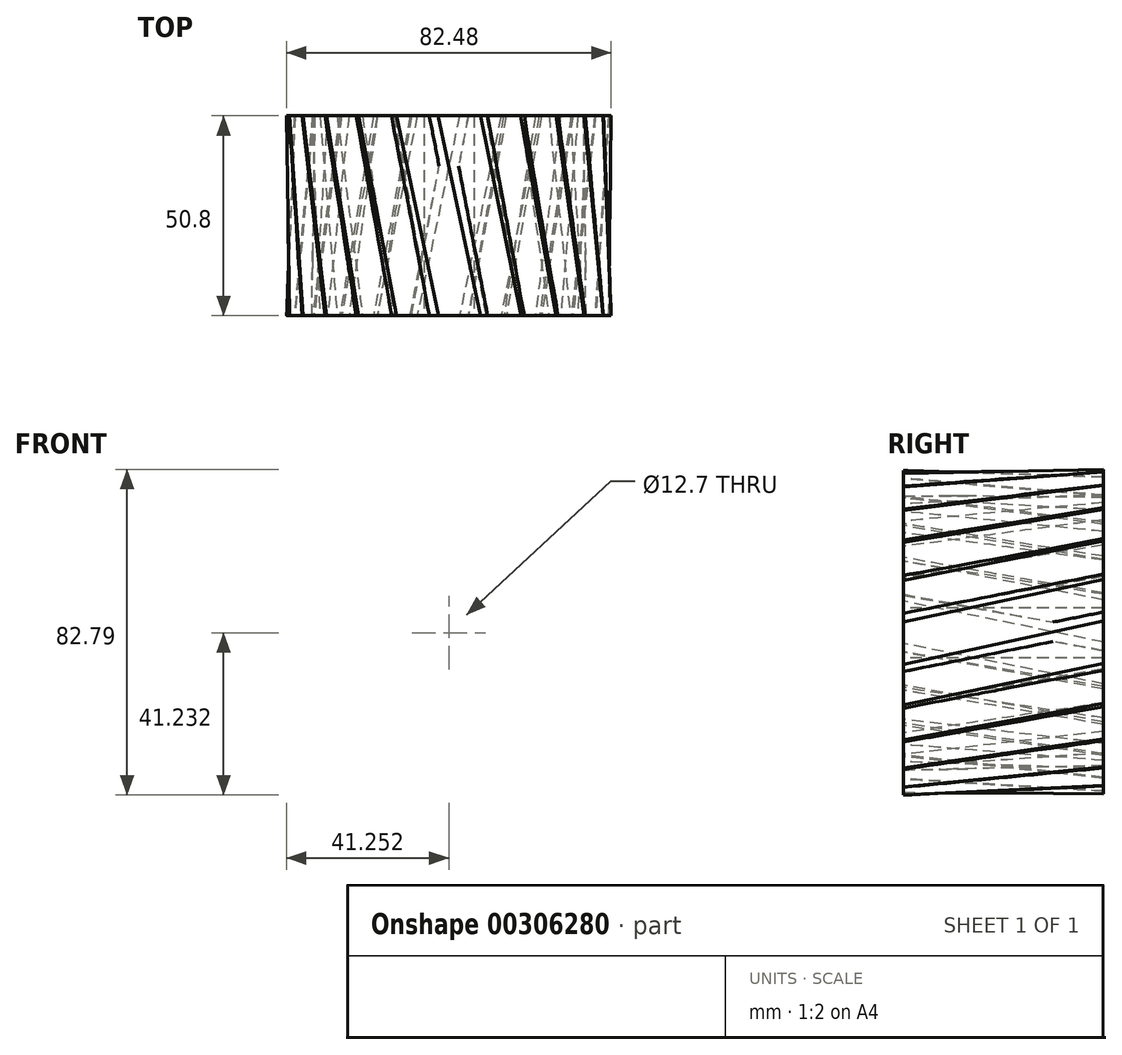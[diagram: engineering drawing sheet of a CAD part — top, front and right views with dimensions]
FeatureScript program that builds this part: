
annotation { "Feature Type Name" : "Feature", "Feature Type Description" : "" }
export const myFeature = defineFeature(function(context is Context, id is Id, definition is map)
    precondition{}
    {
        {
            var Q0;
            Q0=qCreatedBy(makeId("Front.planeOp"),FACE);
            var sketch = newSketch(context, id + "F0", { "sketchPlane" : qUnion([Q0])});
            skArc(sketch, "E0", {"start": v(-6.16, 34.38) * mm, "mid": v(-6.81, 34.25) * mm, "end": v(-7.46, 34.12) * mm});
            skArc(sketch, "E1.trimOffspring", {"start": v(-0.1, 38.36) * mm, "mid": v(-0.85, 39.78) * mm, "end": v(-1.82, 41.06) * mm});
            skLineSegment(sketch, "E2", {"start": v(0.02, 37.85) * mm, "end": v(0.11, 36.37) * mm});
            skLineSegment(sketch, "E3", {"start": v(-2.2, 41.23) * mm, "end": v(-2.7, 41.23) * mm});
            skLineSegment(sketch, "E4.MirrorCS", {"start": v(-3.2, 41.16) * mm, "end": v(-2.7, 41.23) * mm});
            skArc(sketch, "E5.MirrorCS", {"start": v(-4.9, 38.04) * mm, "mid": v(-4.35, 39.55) * mm, "end": v(-3.56, 40.95) * mm});
            skLineSegment(sketch, "E6.MirrorCS", {"start": v(-4.96, 37.52) * mm, "end": v(-4.86, 36.04) * mm});
            skPoint(sketch, "E7.orphan", {"position": v(0.33, 33.11) * mm});
            skPoint(sketch, "E8.orphan", {"position": v(-4.65, 32.79) * mm});
            skPoint(sketch, "E9.visualSharp", {"position": v(0.2, 34.92) * mm});
            skArc(sketch, "E9.filletArc", {"start": v(0.11, 36.37) * mm, "mid": v(0.59, 35.34) * mm, "end": v(1.62, 34.89) * mm});
            skPoint(sketch, "E10.visualSharp", {"position": v(-4.76, 34.6) * mm});
            skArc(sketch, "E10.filletArc", {"start": v(-6.16, 34.38) * mm, "mid": v(-5.2, 34.96) * mm, "end": v(-4.86, 36.04) * mm});
            skPoint(sketch, "E11.visualSharp", {"position": v(-3.43, 41.13) * mm});
            skArc(sketch, "E11.filletArc", {"start": v(-3.2, 41.16) * mm, "mid": v(-3.4, 41.1) * mm, "end": v(-3.56, 40.95) * mm});
            skPoint(sketch, "E12.visualSharp", {"position": v(-1.97, 41.23) * mm});
            skArc(sketch, "E12.filletArc", {"start": v(-1.82, 41.06) * mm, "mid": v(-1.99, 41.18) * mm, "end": v(-2.2, 41.23) * mm});
            skPoint(sketch, "E13.visualSharp", {"position": v(-4.97, 37.77) * mm});
            skArc(sketch, "E13.filletArc", {"start": v(-4.9, 38.04) * mm, "mid": v(-4.95, 37.78) * mm, "end": v(-4.96, 37.52) * mm});
            skPoint(sketch, "E14.visualSharp", {"position": v(0, 38.1) * mm});
            skArc(sketch, "E14.filletArc", {"start": v(0.02, 37.85) * mm, "mid": v(-0.02, 38.1) * mm, "end": v(-0.1, 38.36) * mm});
            skArc(sketch, "E15.1.0", {"start": v(-9.3, 35.16) * mm, "mid": v(-8.58, 34.29) * mm, "end": v(-7.46, 34.12) * mm});
            skArc(sketch, "E15.1.1", {"start": v(-14.85, 31.61) * mm, "mid": v(-14.07, 32.43) * mm, "end": v(-14.02, 33.56) * mm});
            skLineSegment(sketch, "E15.1.2", {"start": v(-9.78, 36.56) * mm, "end": v(-9.3, 35.16) * mm});
            skLineSegment(sketch, "E15.1.3", {"start": v(-14.5, 34.96) * mm, "end": v(-14.02, 33.56) * mm});
            skPoint(sketch, "E15.1.4", {"position": v(-12.58, 39.31) * mm});
            skPoint(sketch, "E15.1.5", {"position": v(-13.96, 38.84) * mm});
            skArc(sketch, "E15.1.6", {"start": v(-14.58, 35.48) * mm, "mid": v(-14.44, 37.08) * mm, "end": v(-14.03, 38.63) * mm});
            skPoint(sketch, "E15.1.7", {"position": v(-14.58, 35.2) * mm});
            skPoint(sketch, "E15.1.8", {"position": v(-9.86, 36.8) * mm});
            skArc(sketch, "E15.1.9", {"start": v(-10.03, 37.02) * mm, "mid": v(-11.11, 38.2) * mm, "end": v(-12.38, 39.2) * mm});
            skLineSegment(sketch, "E15.1.10", {"start": v(-12.79, 39.26) * mm, "end": v(-13.28, 39.12) * mm});
            skLineSegment(sketch, "E15.1.11", {"start": v(-13.75, 38.93) * mm, "end": v(-13.28, 39.12) * mm});
            skArc(sketch, "E15.1.12", {"start": v(-9.78, 36.56) * mm, "mid": v(-9.88, 36.8) * mm, "end": v(-10.03, 37.02) * mm});
            skArc(sketch, "E15.1.13", {"start": v(-13.75, 38.93) * mm, "mid": v(-13.92, 38.8) * mm, "end": v(-14.03, 38.63) * mm});
            skArc(sketch, "E15.1.14", {"start": v(-14.58, 35.48) * mm, "mid": v(-14.56, 35.22) * mm, "end": v(-14.5, 34.96) * mm});
            skArc(sketch, "E15.1.15", {"start": v(-12.38, 39.2) * mm, "mid": v(-12.58, 39.27) * mm, "end": v(-12.79, 39.26) * mm});
            skArc(sketch, "E15.2.0", {"start": v(-18.09, 31.55) * mm, "mid": v(-17.16, 30.9) * mm, "end": v(-16.04, 31.03) * mm});
            skArc(sketch, "E15.2.1", {"start": v(-22.53, 26.69) * mm, "mid": v(-21.98, 27.68) * mm, "end": v(-22.23, 28.78) * mm});
            skLineSegment(sketch, "E15.2.2", {"start": v(-18.9, 32.79) * mm, "end": v(-18.09, 31.55) * mm});
            skLineSegment(sketch, "E15.2.3", {"start": v(-23.05, 30.02) * mm, "end": v(-22.23, 28.78) * mm});
            skPoint(sketch, "E15.2.4", {"position": v(-22.32, 34.72) * mm});
            skPoint(sketch, "E15.2.5", {"position": v(-23.53, 33.9) * mm});
            skArc(sketch, "E15.2.6", {"start": v(-23.27, 30.5) * mm, "mid": v(-23.55, 32.08) * mm, "end": v(-23.55, 33.68) * mm});
            skPoint(sketch, "E15.2.7", {"position": v(-23.2, 30.23) * mm});
            skPoint(sketch, "E15.2.8", {"position": v(-19.05, 33) * mm});
            skArc(sketch, "E15.2.9", {"start": v(-19.27, 33.17) * mm, "mid": v(-20.62, 34.03) * mm, "end": v(-22.1, 34.65) * mm});
            skLineSegment(sketch, "E15.2.10", {"start": v(-22.51, 34.6) * mm, "end": v(-22.95, 34.35) * mm});
            skLineSegment(sketch, "E15.2.11", {"start": v(-23.36, 34.04) * mm, "end": v(-22.95, 34.35) * mm});
            skArc(sketch, "E15.2.12", {"start": v(-18.9, 32.79) * mm, "mid": v(-19.07, 33) * mm, "end": v(-19.27, 33.17) * mm});
            skArc(sketch, "E15.2.13", {"start": v(-23.36, 34.04) * mm, "mid": v(-23.5, 33.88) * mm, "end": v(-23.55, 33.68) * mm});
            skArc(sketch, "E15.2.14", {"start": v(-23.27, 30.5) * mm, "mid": v(-23.18, 30.25) * mm, "end": v(-23.05, 30.02) * mm});
            skArc(sketch, "E15.2.15", {"start": v(-22.1, 34.65) * mm, "mid": v(-22.31, 34.67) * mm, "end": v(-22.51, 34.6) * mm});
            skArc(sketch, "E15.3.0", {"start": v(-25.64, 25.8) * mm, "mid": v(-24.57, 25.4) * mm, "end": v(-23.52, 25.82) * mm});
            skArc(sketch, "E15.3.1", {"start": v(-28.67, 19.95) * mm, "mid": v(-28.4, 21.05) * mm, "end": v(-28.92, 22.05) * mm});
            skLineSegment(sketch, "E15.3.2", {"start": v(-26.75, 26.77) * mm, "end": v(-25.64, 25.8) * mm});
            skLineSegment(sketch, "E15.3.3", {"start": v(-30.04, 23.03) * mm, "end": v(-28.92, 22.05) * mm});
            skPoint(sketch, "E15.3.4", {"position": v(-30.55, 27.76) * mm});
            skPoint(sketch, "E15.3.5", {"position": v(-31.5, 26.66) * mm});
            skArc(sketch, "E15.3.6", {"start": v(-30.37, 23.43) * mm, "mid": v(-31.05, 24.89) * mm, "end": v(-31.47, 26.44) * mm});
            skPoint(sketch, "E15.3.7", {"position": v(-30.23, 23.2) * mm});
            skPoint(sketch, "E15.3.8", {"position": v(-26.94, 26.94) * mm});
            skArc(sketch, "E15.3.9", {"start": v(-27.2, 27.05) * mm, "mid": v(-28.73, 27.53) * mm, "end": v(-30.32, 27.75) * mm});
            skLineSegment(sketch, "E15.3.10", {"start": v(-30.7, 27.6) * mm, "end": v(-31.06, 27.24) * mm});
            skLineSegment(sketch, "E15.3.11", {"start": v(-31.37, 26.84) * mm, "end": v(-31.06, 27.24) * mm});
            skArc(sketch, "E15.3.12", {"start": v(-26.75, 26.77) * mm, "mid": v(-26.96, 26.93) * mm, "end": v(-27.2, 27.05) * mm});
            skArc(sketch, "E15.3.13", {"start": v(-31.37, 26.84) * mm, "mid": v(-31.46, 26.65) * mm, "end": v(-31.47, 26.44) * mm});
            skArc(sketch, "E15.3.14", {"start": v(-30.37, 23.43) * mm, "mid": v(-30.22, 23.22) * mm, "end": v(-30.04, 23.03) * mm});
            skArc(sketch, "E15.3.15", {"start": v(-30.32, 27.75) * mm, "mid": v(-30.53, 27.72) * mm, "end": v(-30.7, 27.6) * mm});
            skArc(sketch, "E15.4.0", {"start": v(-31.44, 18.28) * mm, "mid": v(-30.31, 18.18) * mm, "end": v(-29.4, 18.85) * mm});
            skArc(sketch, "E15.4.1", {"start": v(-32.85, 11.85) * mm, "mid": v(-32.87, 12.98) * mm, "end": v(-33.64, 13.81) * mm});
            skLineSegment(sketch, "E15.4.2", {"start": v(-32.77, 18.94) * mm, "end": v(-31.44, 18.28) * mm});
            skLineSegment(sketch, "E15.4.3", {"start": v(-34.97, 14.47) * mm, "end": v(-33.64, 13.81) * mm});
            skPoint(sketch, "E15.4.4", {"position": v(-36.7, 18.9) * mm});
            skPoint(sketch, "E15.4.5", {"position": v(-37.33, 17.6) * mm});
            skArc(sketch, "E15.4.6", {"start": v(-35.4, 14.77) * mm, "mid": v(-36.43, 16) * mm, "end": v(-37.24, 17.4) * mm});
            skPoint(sketch, "E15.4.7", {"position": v(-35.2, 14.58) * mm});
            skPoint(sketch, "E15.4.8", {"position": v(-33, 19.05) * mm});
            skArc(sketch, "E15.4.9", {"start": v(-33.27, 19.09) * mm, "mid": v(-34.87, 19.16) * mm, "end": v(-36.47, 18.96) * mm});
            skLineSegment(sketch, "E15.4.10", {"start": v(-36.8, 18.71) * mm, "end": v(-37.06, 18.27) * mm});
            skLineSegment(sketch, "E15.4.11", {"start": v(-37.25, 17.8) * mm, "end": v(-37.06, 18.27) * mm});
            skArc(sketch, "E15.4.12", {"start": v(-32.77, 18.94) * mm, "mid": v(-33.01, 19.03) * mm, "end": v(-33.27, 19.09) * mm});
            skArc(sketch, "E15.4.13", {"start": v(-37.25, 17.8) * mm, "mid": v(-37.29, 17.6) * mm, "end": v(-37.24, 17.4) * mm});
            skArc(sketch, "E15.4.14", {"start": v(-35.4, 14.77) * mm, "mid": v(-35.2, 14.6) * mm, "end": v(-34.97, 14.47) * mm});
            skArc(sketch, "E15.4.15", {"start": v(-36.47, 18.96) * mm, "mid": v(-36.66, 18.87) * mm, "end": v(-36.8, 18.71) * mm});
            skArc(sketch, "E15.5.0", {"start": v(-35.1, 9.52) * mm, "mid": v(-33.98, 9.71) * mm, "end": v(-33.28, 10.6) * mm});
            skArc(sketch, "E15.5.1", {"start": v(-34.8, 2.94) * mm, "mid": v(-35.11, 4.03) * mm, "end": v(-36.07, 4.63) * mm});
            skLineSegment(sketch, "E15.5.2", {"start": v(-36.55, 9.81) * mm, "end": v(-35.1, 9.52) * mm});
            skLineSegment(sketch, "E15.5.3", {"start": v(-37.53, 4.92) * mm, "end": v(-36.07, 4.63) * mm});
            skPoint(sketch, "E15.5.4", {"position": v(-40.33, 8.77) * mm});
            skPoint(sketch, "E15.5.5", {"position": v(-40.62, 7.34) * mm});
            skArc(sketch, "E15.5.6", {"start": v(-38.02, 5.1) * mm, "mid": v(-39.33, 6.03) * mm, "end": v(-40.47, 7.16) * mm});
            skPoint(sketch, "E15.5.7", {"position": v(-37.77, 4.97) * mm});
            skPoint(sketch, "E15.5.8", {"position": v(-36.8, 9.86) * mm});
            skArc(sketch, "E15.5.9", {"start": v(-37.08, 9.83) * mm, "mid": v(-38.64, 9.48) * mm, "end": v(-40.13, 8.87) * mm});
            skLineSegment(sketch, "E15.5.10", {"start": v(-40.4, 8.55) * mm, "end": v(-40.52, 8.06) * mm});
            skLineSegment(sketch, "E15.5.11", {"start": v(-40.59, 7.56) * mm, "end": v(-40.52, 8.06) * mm});
            skArc(sketch, "E15.5.12", {"start": v(-36.55, 9.81) * mm, "mid": v(-36.81, 9.84) * mm, "end": v(-37.08, 9.83) * mm});
            skArc(sketch, "E15.5.13", {"start": v(-40.59, 7.56) * mm, "mid": v(-40.57, 7.35) * mm, "end": v(-40.47, 7.16) * mm});
            skArc(sketch, "E15.5.14", {"start": v(-38.02, 5.1) * mm, "mid": v(-37.78, 5) * mm, "end": v(-37.53, 4.92) * mm});
            skArc(sketch, "E15.5.15", {"start": v(-40.13, 8.87) * mm, "mid": v(-40.3, 8.74) * mm, "end": v(-40.4, 8.55) * mm});
            skArc(sketch, "E15.6.0", {"start": v(-36.37, 0.11) * mm, "mid": v(-35.34, 0.59) * mm, "end": v(-34.89, 1.62) * mm});
            skArc(sketch, "E15.6.1", {"start": v(-34.38, -6.16) * mm, "mid": v(-34.96, -5.2) * mm, "end": v(-36.04, -4.86) * mm});
            skLineSegment(sketch, "E15.6.2", {"start": v(-37.85, 0.02) * mm, "end": v(-36.37, 0.11) * mm});
            skLineSegment(sketch, "E15.6.3", {"start": v(-37.52, -4.96) * mm, "end": v(-36.04, -4.86) * mm});
            skPoint(sketch, "E15.6.4", {"position": v(-41.23, -1.97) * mm});
            skPoint(sketch, "E15.6.5", {"position": v(-41.13, -3.43) * mm});
            skArc(sketch, "E15.6.6", {"start": v(-38.04, -4.9) * mm, "mid": v(-39.55, -4.35) * mm, "end": v(-40.95, -3.56) * mm});
            skPoint(sketch, "E15.6.7", {"position": v(-37.77, -4.97) * mm});
            skPoint(sketch, "E15.6.8", {"position": v(-38.1, 0) * mm});
            skArc(sketch, "E15.6.9", {"start": v(-38.36, -0.1) * mm, "mid": v(-39.78, -0.85) * mm, "end": v(-41.06, -1.82) * mm});
            skLineSegment(sketch, "E15.6.10", {"start": v(-41.23, -2.2) * mm, "end": v(-41.23, -2.7) * mm});
            skLineSegment(sketch, "E15.6.11", {"start": v(-41.16, -3.2) * mm, "end": v(-41.23, -2.7) * mm});
            skArc(sketch, "E15.6.12", {"start": v(-37.85, 0.02) * mm, "mid": v(-38.1, -0.02) * mm, "end": v(-38.36, -0.1) * mm});
            skArc(sketch, "E15.6.13", {"start": v(-41.16, -3.2) * mm, "mid": v(-41.1, -3.4) * mm, "end": v(-40.95, -3.56) * mm});
            skArc(sketch, "E15.6.14", {"start": v(-38.04, -4.9) * mm, "mid": v(-37.78, -4.95) * mm, "end": v(-37.52, -4.96) * mm});
            skArc(sketch, "E15.6.15", {"start": v(-41.06, -1.82) * mm, "mid": v(-41.18, -1.99) * mm, "end": v(-41.23, -2.2) * mm});
            skArc(sketch, "E15.7.0", {"start": v(-35.16, -9.3) * mm, "mid": v(-34.29, -8.58) * mm, "end": v(-34.12, -7.46) * mm});
            skArc(sketch, "E15.7.1", {"start": v(-31.61, -14.85) * mm, "mid": v(-32.43, -14.07) * mm, "end": v(-33.56, -14.02) * mm});
            skLineSegment(sketch, "E15.7.2", {"start": v(-36.56, -9.78) * mm, "end": v(-35.16, -9.3) * mm});
            skLineSegment(sketch, "E15.7.3", {"start": v(-34.96, -14.5) * mm, "end": v(-33.56, -14.02) * mm});
            skPoint(sketch, "E15.7.4", {"position": v(-39.31, -12.58) * mm});
            skPoint(sketch, "E15.7.5", {"position": v(-38.84, -13.96) * mm});
            skArc(sketch, "E15.7.6", {"start": v(-35.48, -14.58) * mm, "mid": v(-37.08, -14.44) * mm, "end": v(-38.63, -14.03) * mm});
            skPoint(sketch, "E15.7.7", {"position": v(-35.2, -14.58) * mm});
            skPoint(sketch, "E15.7.8", {"position": v(-36.8, -9.86) * mm});
            skArc(sketch, "E15.7.9", {"start": v(-37.02, -10.03) * mm, "mid": v(-38.2, -11.11) * mm, "end": v(-39.2, -12.38) * mm});
            skLineSegment(sketch, "E15.7.10", {"start": v(-39.26, -12.79) * mm, "end": v(-39.12, -13.28) * mm});
            skLineSegment(sketch, "E15.7.11", {"start": v(-38.93, -13.75) * mm, "end": v(-39.12, -13.28) * mm});
            skArc(sketch, "E15.7.12", {"start": v(-36.56, -9.78) * mm, "mid": v(-36.8, -9.88) * mm, "end": v(-37.02, -10.03) * mm});
            skArc(sketch, "E15.7.13", {"start": v(-38.93, -13.75) * mm, "mid": v(-38.8, -13.92) * mm, "end": v(-38.63, -14.03) * mm});
            skArc(sketch, "E15.7.14", {"start": v(-35.48, -14.58) * mm, "mid": v(-35.22, -14.56) * mm, "end": v(-34.96, -14.5) * mm});
            skArc(sketch, "E15.7.15", {"start": v(-39.2, -12.38) * mm, "mid": v(-39.27, -12.58) * mm, "end": v(-39.26, -12.79) * mm});
            skArc(sketch, "E15.8.0", {"start": v(-31.55, -18.09) * mm, "mid": v(-30.9, -17.16) * mm, "end": v(-31.03, -16.04) * mm});
            skArc(sketch, "E15.8.1", {"start": v(-26.69, -22.53) * mm, "mid": v(-27.68, -21.98) * mm, "end": v(-28.78, -22.23) * mm});
            skLineSegment(sketch, "E15.8.2", {"start": v(-32.79, -18.9) * mm, "end": v(-31.55, -18.09) * mm});
            skLineSegment(sketch, "E15.8.3", {"start": v(-30.02, -23.05) * mm, "end": v(-28.78, -22.23) * mm});
            skPoint(sketch, "E15.8.4", {"position": v(-34.72, -22.32) * mm});
            skPoint(sketch, "E15.8.5", {"position": v(-33.9, -23.53) * mm});
            skArc(sketch, "E15.8.6", {"start": v(-30.5, -23.27) * mm, "mid": v(-32.08, -23.55) * mm, "end": v(-33.68, -23.55) * mm});
            skPoint(sketch, "E15.8.7", {"position": v(-30.23, -23.2) * mm});
            skPoint(sketch, "E15.8.8", {"position": v(-33, -19.05) * mm});
            skArc(sketch, "E15.8.9", {"start": v(-33.17, -19.27) * mm, "mid": v(-34.03, -20.62) * mm, "end": v(-34.65, -22.1) * mm});
            skLineSegment(sketch, "E15.8.10", {"start": v(-34.6, -22.51) * mm, "end": v(-34.35, -22.95) * mm});
            skLineSegment(sketch, "E15.8.11", {"start": v(-34.04, -23.36) * mm, "end": v(-34.35, -22.95) * mm});
            skArc(sketch, "E15.8.12", {"start": v(-32.79, -18.9) * mm, "mid": v(-33, -19.07) * mm, "end": v(-33.17, -19.27) * mm});
            skArc(sketch, "E15.8.13", {"start": v(-34.04, -23.36) * mm, "mid": v(-33.88, -23.5) * mm, "end": v(-33.68, -23.55) * mm});
            skArc(sketch, "E15.8.14", {"start": v(-30.5, -23.27) * mm, "mid": v(-30.25, -23.18) * mm, "end": v(-30.02, -23.05) * mm});
            skArc(sketch, "E15.8.15", {"start": v(-34.65, -22.1) * mm, "mid": v(-34.67, -22.31) * mm, "end": v(-34.6, -22.51) * mm});
            skArc(sketch, "E15.9.0", {"start": v(-25.8, -25.64) * mm, "mid": v(-25.4, -24.57) * mm, "end": v(-25.82, -23.52) * mm});
            skArc(sketch, "E15.9.1", {"start": v(-19.95, -28.67) * mm, "mid": v(-21.05, -28.4) * mm, "end": v(-22.05, -28.92) * mm});
            skLineSegment(sketch, "E15.9.2", {"start": v(-26.77, -26.75) * mm, "end": v(-25.8, -25.64) * mm});
            skLineSegment(sketch, "E15.9.3", {"start": v(-23.03, -30.04) * mm, "end": v(-22.05, -28.92) * mm});
            skPoint(sketch, "E15.9.4", {"position": v(-27.76, -30.55) * mm});
            skPoint(sketch, "E15.9.5", {"position": v(-26.66, -31.5) * mm});
            skArc(sketch, "E15.9.6", {"start": v(-23.43, -30.37) * mm, "mid": v(-24.89, -31.05) * mm, "end": v(-26.44, -31.47) * mm});
            skPoint(sketch, "E15.9.7", {"position": v(-23.2, -30.23) * mm});
            skPoint(sketch, "E15.9.8", {"position": v(-26.94, -26.94) * mm});
            skArc(sketch, "E15.9.9", {"start": v(-27.05, -27.2) * mm, "mid": v(-27.53, -28.73) * mm, "end": v(-27.75, -30.32) * mm});
            skLineSegment(sketch, "E15.9.10", {"start": v(-27.6, -30.7) * mm, "end": v(-27.24, -31.06) * mm});
            skLineSegment(sketch, "E15.9.11", {"start": v(-26.84, -31.37) * mm, "end": v(-27.24, -31.06) * mm});
            skArc(sketch, "E15.9.12", {"start": v(-26.77, -26.75) * mm, "mid": v(-26.93, -26.96) * mm, "end": v(-27.05, -27.2) * mm});
            skArc(sketch, "E15.9.13", {"start": v(-26.84, -31.37) * mm, "mid": v(-26.65, -31.46) * mm, "end": v(-26.44, -31.47) * mm});
            skArc(sketch, "E15.9.14", {"start": v(-23.43, -30.37) * mm, "mid": v(-23.22, -30.22) * mm, "end": v(-23.03, -30.04) * mm});
            skArc(sketch, "E15.9.15", {"start": v(-27.75, -30.32) * mm, "mid": v(-27.72, -30.53) * mm, "end": v(-27.6, -30.7) * mm});
            skArc(sketch, "E15.10.0", {"start": v(-18.28, -31.44) * mm, "mid": v(-18.18, -30.31) * mm, "end": v(-18.85, -29.4) * mm});
            skArc(sketch, "E15.10.1", {"start": v(-11.85, -32.85) * mm, "mid": v(-12.98, -32.87) * mm, "end": v(-13.81, -33.64) * mm});
            skLineSegment(sketch, "E15.10.2", {"start": v(-18.94, -32.77) * mm, "end": v(-18.28, -31.44) * mm});
            skLineSegment(sketch, "E15.10.3", {"start": v(-14.47, -34.97) * mm, "end": v(-13.81, -33.64) * mm});
            skPoint(sketch, "E15.10.4", {"position": v(-18.9, -36.7) * mm});
            skPoint(sketch, "E15.10.5", {"position": v(-17.6, -37.33) * mm});
            skArc(sketch, "E15.10.6", {"start": v(-14.77, -35.4) * mm, "mid": v(-16, -36.43) * mm, "end": v(-17.4, -37.24) * mm});
            skPoint(sketch, "E15.10.7", {"position": v(-14.58, -35.2) * mm});
            skPoint(sketch, "E15.10.8", {"position": v(-19.05, -33) * mm});
            skArc(sketch, "E15.10.9", {"start": v(-19.09, -33.27) * mm, "mid": v(-19.16, -34.87) * mm, "end": v(-18.96, -36.47) * mm});
            skLineSegment(sketch, "E15.10.10", {"start": v(-18.71, -36.8) * mm, "end": v(-18.27, -37.06) * mm});
            skLineSegment(sketch, "E15.10.11", {"start": v(-17.8, -37.25) * mm, "end": v(-18.27, -37.06) * mm});
            skArc(sketch, "E15.10.12", {"start": v(-18.94, -32.77) * mm, "mid": v(-19.03, -33.01) * mm, "end": v(-19.09, -33.27) * mm});
            skArc(sketch, "E15.10.13", {"start": v(-17.8, -37.25) * mm, "mid": v(-17.6, -37.29) * mm, "end": v(-17.4, -37.24) * mm});
            skArc(sketch, "E15.10.14", {"start": v(-14.77, -35.4) * mm, "mid": v(-14.6, -35.2) * mm, "end": v(-14.47, -34.97) * mm});
            skArc(sketch, "E15.10.15", {"start": v(-18.96, -36.47) * mm, "mid": v(-18.87, -36.66) * mm, "end": v(-18.71, -36.8) * mm});
            skArc(sketch, "E15.11.0", {"start": v(-9.52, -35.1) * mm, "mid": v(-9.71, -33.98) * mm, "end": v(-10.6, -33.28) * mm});
            skArc(sketch, "E15.11.1", {"start": v(-2.94, -34.8) * mm, "mid": v(-4.03, -35.11) * mm, "end": v(-4.63, -36.07) * mm});
            skLineSegment(sketch, "E15.11.2", {"start": v(-9.81, -36.55) * mm, "end": v(-9.52, -35.1) * mm});
            skLineSegment(sketch, "E15.11.3", {"start": v(-4.92, -37.53) * mm, "end": v(-4.63, -36.07) * mm});
            skPoint(sketch, "E15.11.4", {"position": v(-8.77, -40.33) * mm});
            skPoint(sketch, "E15.11.5", {"position": v(-7.34, -40.62) * mm});
            skArc(sketch, "E15.11.6", {"start": v(-5.1, -38.02) * mm, "mid": v(-6.03, -39.33) * mm, "end": v(-7.16, -40.47) * mm});
            skPoint(sketch, "E15.11.7", {"position": v(-4.97, -37.77) * mm});
            skPoint(sketch, "E15.11.8", {"position": v(-9.86, -36.8) * mm});
            skArc(sketch, "E15.11.9", {"start": v(-9.83, -37.08) * mm, "mid": v(-9.48, -38.64) * mm, "end": v(-8.87, -40.13) * mm});
            skLineSegment(sketch, "E15.11.10", {"start": v(-8.55, -40.4) * mm, "end": v(-8.06, -40.52) * mm});
            skLineSegment(sketch, "E15.11.11", {"start": v(-7.56, -40.59) * mm, "end": v(-8.06, -40.52) * mm});
            skArc(sketch, "E15.11.12", {"start": v(-9.81, -36.55) * mm, "mid": v(-9.84, -36.81) * mm, "end": v(-9.83, -37.08) * mm});
            skArc(sketch, "E15.11.13", {"start": v(-7.56, -40.59) * mm, "mid": v(-7.35, -40.57) * mm, "end": v(-7.16, -40.47) * mm});
            skArc(sketch, "E15.11.14", {"start": v(-5.1, -38.02) * mm, "mid": v(-5, -37.78) * mm, "end": v(-4.92, -37.53) * mm});
            skArc(sketch, "E15.11.15", {"start": v(-8.87, -40.13) * mm, "mid": v(-8.74, -40.3) * mm, "end": v(-8.55, -40.4) * mm});
            skArc(sketch, "E15.12.0", {"start": v(-0.11, -36.37) * mm, "mid": v(-0.59, -35.34) * mm, "end": v(-1.62, -34.89) * mm});
            skArc(sketch, "E15.12.1", {"start": v(6.16, -34.38) * mm, "mid": v(5.2, -34.96) * mm, "end": v(4.86, -36.04) * mm});
            skLineSegment(sketch, "E15.12.2", {"start": v(-0.02, -37.85) * mm, "end": v(-0.11, -36.37) * mm});
            skLineSegment(sketch, "E15.12.3", {"start": v(4.96, -37.52) * mm, "end": v(4.86, -36.04) * mm});
            skPoint(sketch, "E15.12.4", {"position": v(1.97, -41.23) * mm});
            skPoint(sketch, "E15.12.5", {"position": v(3.43, -41.13) * mm});
            skArc(sketch, "E15.12.6", {"start": v(4.9, -38.04) * mm, "mid": v(4.35, -39.55) * mm, "end": v(3.56, -40.95) * mm});
            skPoint(sketch, "E15.12.7", {"position": v(4.97, -37.77) * mm});
            skPoint(sketch, "E15.12.8", {"position": v(0, -38.1) * mm});
            skArc(sketch, "E15.12.9", {"start": v(0.1, -38.36) * mm, "mid": v(0.85, -39.78) * mm, "end": v(1.82, -41.06) * mm});
            skLineSegment(sketch, "E15.12.10", {"start": v(2.2, -41.23) * mm, "end": v(2.7, -41.23) * mm});
            skLineSegment(sketch, "E15.12.11", {"start": v(3.2, -41.16) * mm, "end": v(2.7, -41.23) * mm});
            skArc(sketch, "E15.12.12", {"start": v(-0.02, -37.85) * mm, "mid": v(0.02, -38.1) * mm, "end": v(0.1, -38.36) * mm});
            skArc(sketch, "E15.12.13", {"start": v(3.2, -41.16) * mm, "mid": v(3.4, -41.1) * mm, "end": v(3.56, -40.95) * mm});
            skArc(sketch, "E15.12.14", {"start": v(4.9, -38.04) * mm, "mid": v(4.95, -37.78) * mm, "end": v(4.96, -37.52) * mm});
            skArc(sketch, "E15.12.15", {"start": v(1.82, -41.06) * mm, "mid": v(1.99, -41.18) * mm, "end": v(2.2, -41.23) * mm});
            skArc(sketch, "E15.13.0", {"start": v(9.3, -35.16) * mm, "mid": v(8.58, -34.29) * mm, "end": v(7.46, -34.12) * mm});
            skArc(sketch, "E15.13.1", {"start": v(14.85, -31.61) * mm, "mid": v(14.07, -32.43) * mm, "end": v(14.02, -33.56) * mm});
            skLineSegment(sketch, "E15.13.2", {"start": v(9.78, -36.56) * mm, "end": v(9.3, -35.16) * mm});
            skLineSegment(sketch, "E15.13.3", {"start": v(14.5, -34.96) * mm, "end": v(14.02, -33.56) * mm});
            skPoint(sketch, "E15.13.4", {"position": v(12.58, -39.31) * mm});
            skPoint(sketch, "E15.13.5", {"position": v(13.96, -38.84) * mm});
            skArc(sketch, "E15.13.6", {"start": v(14.58, -35.48) * mm, "mid": v(14.44, -37.08) * mm, "end": v(14.03, -38.63) * mm});
            skPoint(sketch, "E15.13.7", {"position": v(14.58, -35.2) * mm});
            skPoint(sketch, "E15.13.8", {"position": v(9.86, -36.8) * mm});
            skArc(sketch, "E15.13.9", {"start": v(10.03, -37.02) * mm, "mid": v(11.11, -38.2) * mm, "end": v(12.38, -39.2) * mm});
            skLineSegment(sketch, "E15.13.10", {"start": v(12.79, -39.26) * mm, "end": v(13.28, -39.12) * mm});
            skLineSegment(sketch, "E15.13.11", {"start": v(13.75, -38.93) * mm, "end": v(13.28, -39.12) * mm});
            skArc(sketch, "E15.13.12", {"start": v(9.78, -36.56) * mm, "mid": v(9.88, -36.8) * mm, "end": v(10.03, -37.02) * mm});
            skArc(sketch, "E15.13.13", {"start": v(13.75, -38.93) * mm, "mid": v(13.92, -38.8) * mm, "end": v(14.03, -38.63) * mm});
            skArc(sketch, "E15.13.14", {"start": v(14.58, -35.48) * mm, "mid": v(14.56, -35.22) * mm, "end": v(14.5, -34.96) * mm});
            skArc(sketch, "E15.13.15", {"start": v(12.38, -39.2) * mm, "mid": v(12.58, -39.27) * mm, "end": v(12.79, -39.26) * mm});
            skArc(sketch, "E15.14.0", {"start": v(18.09, -31.55) * mm, "mid": v(17.16, -30.9) * mm, "end": v(16.04, -31.03) * mm});
            skArc(sketch, "E15.14.1", {"start": v(22.53, -26.69) * mm, "mid": v(21.98, -27.68) * mm, "end": v(22.23, -28.78) * mm});
            skLineSegment(sketch, "E15.14.2", {"start": v(18.9, -32.79) * mm, "end": v(18.09, -31.55) * mm});
            skLineSegment(sketch, "E15.14.3", {"start": v(23.05, -30.02) * mm, "end": v(22.23, -28.78) * mm});
            skPoint(sketch, "E15.14.4", {"position": v(22.32, -34.72) * mm});
            skPoint(sketch, "E15.14.5", {"position": v(23.53, -33.9) * mm});
            skArc(sketch, "E15.14.6", {"start": v(23.27, -30.5) * mm, "mid": v(23.55, -32.08) * mm, "end": v(23.55, -33.68) * mm});
            skPoint(sketch, "E15.14.7", {"position": v(23.2, -30.23) * mm});
            skPoint(sketch, "E15.14.8", {"position": v(19.05, -33) * mm});
            skArc(sketch, "E15.14.9", {"start": v(19.27, -33.17) * mm, "mid": v(20.62, -34.03) * mm, "end": v(22.1, -34.65) * mm});
            skLineSegment(sketch, "E15.14.10", {"start": v(22.51, -34.6) * mm, "end": v(22.95, -34.35) * mm});
            skLineSegment(sketch, "E15.14.11", {"start": v(23.36, -34.04) * mm, "end": v(22.95, -34.35) * mm});
            skArc(sketch, "E15.14.12", {"start": v(18.9, -32.79) * mm, "mid": v(19.07, -33) * mm, "end": v(19.27, -33.17) * mm});
            skArc(sketch, "E15.14.13", {"start": v(23.36, -34.04) * mm, "mid": v(23.5, -33.88) * mm, "end": v(23.55, -33.68) * mm});
            skArc(sketch, "E15.14.14", {"start": v(23.27, -30.5) * mm, "mid": v(23.18, -30.25) * mm, "end": v(23.05, -30.02) * mm});
            skArc(sketch, "E15.14.15", {"start": v(22.1, -34.65) * mm, "mid": v(22.31, -34.67) * mm, "end": v(22.51, -34.6) * mm});
            skArc(sketch, "E15.15.0", {"start": v(25.64, -25.8) * mm, "mid": v(24.57, -25.4) * mm, "end": v(23.52, -25.82) * mm});
            skArc(sketch, "E15.15.1", {"start": v(28.67, -19.95) * mm, "mid": v(28.4, -21.05) * mm, "end": v(28.92, -22.05) * mm});
            skLineSegment(sketch, "E15.15.2", {"start": v(26.75, -26.77) * mm, "end": v(25.64, -25.8) * mm});
            skLineSegment(sketch, "E15.15.3", {"start": v(30.04, -23.03) * mm, "end": v(28.92, -22.05) * mm});
            skPoint(sketch, "E15.15.4", {"position": v(30.55, -27.76) * mm});
            skPoint(sketch, "E15.15.5", {"position": v(31.5, -26.66) * mm});
            skArc(sketch, "E15.15.6", {"start": v(30.37, -23.43) * mm, "mid": v(31.05, -24.89) * mm, "end": v(31.47, -26.44) * mm});
            skPoint(sketch, "E15.15.7", {"position": v(30.23, -23.2) * mm});
            skPoint(sketch, "E15.15.8", {"position": v(26.94, -26.94) * mm});
            skArc(sketch, "E15.15.9", {"start": v(27.2, -27.05) * mm, "mid": v(28.73, -27.53) * mm, "end": v(30.32, -27.75) * mm});
            skLineSegment(sketch, "E15.15.10", {"start": v(30.7, -27.6) * mm, "end": v(31.06, -27.24) * mm});
            skLineSegment(sketch, "E15.15.11", {"start": v(31.37, -26.84) * mm, "end": v(31.06, -27.24) * mm});
            skArc(sketch, "E15.15.12", {"start": v(26.75, -26.77) * mm, "mid": v(26.96, -26.93) * mm, "end": v(27.2, -27.05) * mm});
            skArc(sketch, "E15.15.13", {"start": v(31.37, -26.84) * mm, "mid": v(31.46, -26.65) * mm, "end": v(31.47, -26.44) * mm});
            skArc(sketch, "E15.15.14", {"start": v(30.37, -23.43) * mm, "mid": v(30.22, -23.22) * mm, "end": v(30.04, -23.03) * mm});
            skArc(sketch, "E15.15.15", {"start": v(30.32, -27.75) * mm, "mid": v(30.53, -27.72) * mm, "end": v(30.7, -27.6) * mm});
            skArc(sketch, "E15.16.0", {"start": v(31.44, -18.28) * mm, "mid": v(30.31, -18.18) * mm, "end": v(29.4, -18.85) * mm});
            skArc(sketch, "E15.16.1", {"start": v(32.85, -11.85) * mm, "mid": v(32.87, -12.98) * mm, "end": v(33.64, -13.81) * mm});
            skLineSegment(sketch, "E15.16.2", {"start": v(32.77, -18.94) * mm, "end": v(31.44, -18.28) * mm});
            skLineSegment(sketch, "E15.16.3", {"start": v(34.97, -14.47) * mm, "end": v(33.64, -13.81) * mm});
            skPoint(sketch, "E15.16.4", {"position": v(36.7, -18.9) * mm});
            skPoint(sketch, "E15.16.5", {"position": v(37.33, -17.6) * mm});
            skArc(sketch, "E15.16.6", {"start": v(35.4, -14.77) * mm, "mid": v(36.43, -16) * mm, "end": v(37.24, -17.4) * mm});
            skPoint(sketch, "E15.16.7", {"position": v(35.2, -14.58) * mm});
            skPoint(sketch, "E15.16.8", {"position": v(33, -19.05) * mm});
            skArc(sketch, "E15.16.9", {"start": v(33.27, -19.09) * mm, "mid": v(34.87, -19.16) * mm, "end": v(36.47, -18.96) * mm});
            skLineSegment(sketch, "E15.16.10", {"start": v(36.8, -18.71) * mm, "end": v(37.06, -18.27) * mm});
            skLineSegment(sketch, "E15.16.11", {"start": v(37.25, -17.8) * mm, "end": v(37.06, -18.27) * mm});
            skArc(sketch, "E15.16.12", {"start": v(32.77, -18.94) * mm, "mid": v(33.01, -19.03) * mm, "end": v(33.27, -19.09) * mm});
            skArc(sketch, "E15.16.13", {"start": v(37.25, -17.8) * mm, "mid": v(37.29, -17.6) * mm, "end": v(37.24, -17.4) * mm});
            skArc(sketch, "E15.16.14", {"start": v(35.4, -14.77) * mm, "mid": v(35.2, -14.6) * mm, "end": v(34.97, -14.47) * mm});
            skArc(sketch, "E15.16.15", {"start": v(36.47, -18.96) * mm, "mid": v(36.66, -18.87) * mm, "end": v(36.8, -18.71) * mm});
            skArc(sketch, "E15.17.0", {"start": v(35.1, -9.52) * mm, "mid": v(33.98, -9.71) * mm, "end": v(33.28, -10.6) * mm});
            skArc(sketch, "E15.17.1", {"start": v(34.8, -2.94) * mm, "mid": v(35.11, -4.03) * mm, "end": v(36.07, -4.63) * mm});
            skLineSegment(sketch, "E15.17.2", {"start": v(36.55, -9.81) * mm, "end": v(35.1, -9.52) * mm});
            skLineSegment(sketch, "E15.17.3", {"start": v(37.53, -4.92) * mm, "end": v(36.07, -4.63) * mm});
            skPoint(sketch, "E15.17.4", {"position": v(40.33, -8.77) * mm});
            skPoint(sketch, "E15.17.5", {"position": v(40.62, -7.34) * mm});
            skArc(sketch, "E15.17.6", {"start": v(38.02, -5.1) * mm, "mid": v(39.33, -6.03) * mm, "end": v(40.47, -7.16) * mm});
            skPoint(sketch, "E15.17.7", {"position": v(37.77, -4.97) * mm});
            skPoint(sketch, "E15.17.8", {"position": v(36.8, -9.86) * mm});
            skArc(sketch, "E15.17.9", {"start": v(37.08, -9.83) * mm, "mid": v(38.64, -9.48) * mm, "end": v(40.13, -8.87) * mm});
            skLineSegment(sketch, "E15.17.10", {"start": v(40.4, -8.55) * mm, "end": v(40.52, -8.06) * mm});
            skLineSegment(sketch, "E15.17.11", {"start": v(40.59, -7.56) * mm, "end": v(40.52, -8.06) * mm});
            skArc(sketch, "E15.17.12", {"start": v(36.55, -9.81) * mm, "mid": v(36.81, -9.84) * mm, "end": v(37.08, -9.83) * mm});
            skArc(sketch, "E15.17.13", {"start": v(40.59, -7.56) * mm, "mid": v(40.57, -7.35) * mm, "end": v(40.47, -7.16) * mm});
            skArc(sketch, "E15.17.14", {"start": v(38.02, -5.1) * mm, "mid": v(37.78, -5) * mm, "end": v(37.53, -4.92) * mm});
            skArc(sketch, "E15.17.15", {"start": v(40.13, -8.87) * mm, "mid": v(40.3, -8.74) * mm, "end": v(40.4, -8.55) * mm});
            skArc(sketch, "E15.18.0", {"start": v(36.37, -0.11) * mm, "mid": v(35.34, -0.59) * mm, "end": v(34.89, -1.62) * mm});
            skArc(sketch, "E15.18.1", {"start": v(34.38, 6.16) * mm, "mid": v(34.96, 5.2) * mm, "end": v(36.04, 4.86) * mm});
            skLineSegment(sketch, "E15.18.2", {"start": v(37.85, -0.02) * mm, "end": v(36.37, -0.11) * mm});
            skLineSegment(sketch, "E15.18.3", {"start": v(37.52, 4.96) * mm, "end": v(36.04, 4.86) * mm});
            skPoint(sketch, "E15.18.4", {"position": v(41.23, 1.97) * mm});
            skPoint(sketch, "E15.18.5", {"position": v(41.13, 3.43) * mm});
            skArc(sketch, "E15.18.6", {"start": v(38.04, 4.9) * mm, "mid": v(39.55, 4.35) * mm, "end": v(40.95, 3.56) * mm});
            skPoint(sketch, "E15.18.7", {"position": v(37.77, 4.97) * mm});
            skPoint(sketch, "E15.18.8", {"position": v(38.1, 0) * mm});
            skArc(sketch, "E15.18.9", {"start": v(38.36, 0.1) * mm, "mid": v(39.78, 0.85) * mm, "end": v(41.06, 1.82) * mm});
            skLineSegment(sketch, "E15.18.10", {"start": v(41.23, 2.2) * mm, "end": v(41.23, 2.7) * mm});
            skLineSegment(sketch, "E15.18.11", {"start": v(41.16, 3.2) * mm, "end": v(41.23, 2.7) * mm});
            skArc(sketch, "E15.18.12", {"start": v(37.85, -0.02) * mm, "mid": v(38.1, 0.02) * mm, "end": v(38.36, 0.1) * mm});
            skArc(sketch, "E15.18.13", {"start": v(41.16, 3.2) * mm, "mid": v(41.1, 3.4) * mm, "end": v(40.95, 3.56) * mm});
            skArc(sketch, "E15.18.14", {"start": v(38.04, 4.9) * mm, "mid": v(37.78, 4.95) * mm, "end": v(37.52, 4.96) * mm});
            skArc(sketch, "E15.18.15", {"start": v(41.06, 1.82) * mm, "mid": v(41.18, 1.99) * mm, "end": v(41.23, 2.2) * mm});
            skArc(sketch, "E15.19.0", {"start": v(35.16, 9.3) * mm, "mid": v(34.29, 8.58) * mm, "end": v(34.12, 7.46) * mm});
            skArc(sketch, "E15.19.1", {"start": v(31.61, 14.85) * mm, "mid": v(32.43, 14.07) * mm, "end": v(33.56, 14.02) * mm});
            skLineSegment(sketch, "E15.19.2", {"start": v(36.56, 9.78) * mm, "end": v(35.16, 9.3) * mm});
            skLineSegment(sketch, "E15.19.3", {"start": v(34.96, 14.5) * mm, "end": v(33.56, 14.02) * mm});
            skPoint(sketch, "E15.19.4", {"position": v(39.31, 12.58) * mm});
            skPoint(sketch, "E15.19.5", {"position": v(38.84, 13.96) * mm});
            skArc(sketch, "E15.19.6", {"start": v(35.48, 14.58) * mm, "mid": v(37.08, 14.44) * mm, "end": v(38.63, 14.03) * mm});
            skPoint(sketch, "E15.19.7", {"position": v(35.2, 14.58) * mm});
            skPoint(sketch, "E15.19.8", {"position": v(36.8, 9.86) * mm});
            skArc(sketch, "E15.19.9", {"start": v(37.02, 10.03) * mm, "mid": v(38.2, 11.11) * mm, "end": v(39.2, 12.38) * mm});
            skLineSegment(sketch, "E15.19.10", {"start": v(39.26, 12.79) * mm, "end": v(39.12, 13.28) * mm});
            skLineSegment(sketch, "E15.19.11", {"start": v(38.93, 13.75) * mm, "end": v(39.12, 13.28) * mm});
            skArc(sketch, "E15.19.12", {"start": v(36.56, 9.78) * mm, "mid": v(36.8, 9.88) * mm, "end": v(37.02, 10.03) * mm});
            skArc(sketch, "E15.19.13", {"start": v(38.93, 13.75) * mm, "mid": v(38.8, 13.92) * mm, "end": v(38.63, 14.03) * mm});
            skArc(sketch, "E15.19.14", {"start": v(35.48, 14.58) * mm, "mid": v(35.22, 14.56) * mm, "end": v(34.96, 14.5) * mm});
            skArc(sketch, "E15.19.15", {"start": v(39.2, 12.38) * mm, "mid": v(39.27, 12.58) * mm, "end": v(39.26, 12.79) * mm});
            skArc(sketch, "E15.20.0", {"start": v(31.55, 18.09) * mm, "mid": v(30.9, 17.16) * mm, "end": v(31.03, 16.04) * mm});
            skArc(sketch, "E15.20.1", {"start": v(26.69, 22.53) * mm, "mid": v(27.68, 21.98) * mm, "end": v(28.78, 22.23) * mm});
            skLineSegment(sketch, "E15.20.2", {"start": v(32.79, 18.9) * mm, "end": v(31.55, 18.09) * mm});
            skLineSegment(sketch, "E15.20.3", {"start": v(30.02, 23.05) * mm, "end": v(28.78, 22.23) * mm});
            skPoint(sketch, "E15.20.4", {"position": v(34.72, 22.32) * mm});
            skPoint(sketch, "E15.20.5", {"position": v(33.9, 23.53) * mm});
            skArc(sketch, "E15.20.6", {"start": v(30.5, 23.27) * mm, "mid": v(32.08, 23.55) * mm, "end": v(33.68, 23.55) * mm});
            skPoint(sketch, "E15.20.7", {"position": v(30.23, 23.2) * mm});
            skPoint(sketch, "E15.20.8", {"position": v(33, 19.05) * mm});
            skArc(sketch, "E15.20.9", {"start": v(33.17, 19.27) * mm, "mid": v(34.03, 20.62) * mm, "end": v(34.65, 22.1) * mm});
            skLineSegment(sketch, "E15.20.10", {"start": v(34.6, 22.51) * mm, "end": v(34.35, 22.95) * mm});
            skLineSegment(sketch, "E15.20.11", {"start": v(34.04, 23.36) * mm, "end": v(34.35, 22.95) * mm});
            skArc(sketch, "E15.20.12", {"start": v(32.79, 18.9) * mm, "mid": v(33, 19.07) * mm, "end": v(33.17, 19.27) * mm});
            skArc(sketch, "E15.20.13", {"start": v(34.04, 23.36) * mm, "mid": v(33.88, 23.5) * mm, "end": v(33.68, 23.55) * mm});
            skArc(sketch, "E15.20.14", {"start": v(30.5, 23.27) * mm, "mid": v(30.25, 23.18) * mm, "end": v(30.02, 23.05) * mm});
            skArc(sketch, "E15.20.15", {"start": v(34.65, 22.1) * mm, "mid": v(34.67, 22.31) * mm, "end": v(34.6, 22.51) * mm});
            skArc(sketch, "E15.21.0", {"start": v(25.8, 25.64) * mm, "mid": v(25.4, 24.57) * mm, "end": v(25.82, 23.52) * mm});
            skArc(sketch, "E15.21.1", {"start": v(19.95, 28.67) * mm, "mid": v(21.05, 28.4) * mm, "end": v(22.05, 28.92) * mm});
            skLineSegment(sketch, "E15.21.2", {"start": v(26.77, 26.75) * mm, "end": v(25.8, 25.64) * mm});
            skLineSegment(sketch, "E15.21.3", {"start": v(23.03, 30.04) * mm, "end": v(22.05, 28.92) * mm});
            skPoint(sketch, "E15.21.4", {"position": v(27.76, 30.55) * mm});
            skPoint(sketch, "E15.21.5", {"position": v(26.66, 31.5) * mm});
            skArc(sketch, "E15.21.6", {"start": v(23.43, 30.37) * mm, "mid": v(24.89, 31.05) * mm, "end": v(26.44, 31.47) * mm});
            skPoint(sketch, "E15.21.7", {"position": v(23.2, 30.23) * mm});
            skPoint(sketch, "E15.21.8", {"position": v(26.94, 26.94) * mm});
            skArc(sketch, "E15.21.9", {"start": v(27.05, 27.2) * mm, "mid": v(27.53, 28.73) * mm, "end": v(27.75, 30.32) * mm});
            skLineSegment(sketch, "E15.21.10", {"start": v(27.6, 30.7) * mm, "end": v(27.24, 31.06) * mm});
            skLineSegment(sketch, "E15.21.11", {"start": v(26.84, 31.37) * mm, "end": v(27.24, 31.06) * mm});
            skArc(sketch, "E15.21.12", {"start": v(26.77, 26.75) * mm, "mid": v(26.93, 26.96) * mm, "end": v(27.05, 27.2) * mm});
            skArc(sketch, "E15.21.13", {"start": v(26.84, 31.37) * mm, "mid": v(26.65, 31.46) * mm, "end": v(26.44, 31.47) * mm});
            skArc(sketch, "E15.21.14", {"start": v(23.43, 30.37) * mm, "mid": v(23.22, 30.22) * mm, "end": v(23.03, 30.04) * mm});
            skArc(sketch, "E15.21.15", {"start": v(27.75, 30.32) * mm, "mid": v(27.72, 30.53) * mm, "end": v(27.6, 30.7) * mm});
            skArc(sketch, "E15.22.0", {"start": v(18.28, 31.44) * mm, "mid": v(18.18, 30.31) * mm, "end": v(18.85, 29.4) * mm});
            skArc(sketch, "E15.22.1", {"start": v(11.85, 32.85) * mm, "mid": v(12.98, 32.87) * mm, "end": v(13.81, 33.64) * mm});
            skLineSegment(sketch, "E15.22.2", {"start": v(18.94, 32.77) * mm, "end": v(18.28, 31.44) * mm});
            skLineSegment(sketch, "E15.22.3", {"start": v(14.47, 34.97) * mm, "end": v(13.81, 33.64) * mm});
            skPoint(sketch, "E15.22.4", {"position": v(18.9, 36.7) * mm});
            skPoint(sketch, "E15.22.5", {"position": v(17.6, 37.33) * mm});
            skArc(sketch, "E15.22.6", {"start": v(14.77, 35.4) * mm, "mid": v(16, 36.43) * mm, "end": v(17.4, 37.24) * mm});
            skPoint(sketch, "E15.22.7", {"position": v(14.58, 35.2) * mm});
            skPoint(sketch, "E15.22.8", {"position": v(19.05, 33) * mm});
            skArc(sketch, "E15.22.9", {"start": v(19.09, 33.27) * mm, "mid": v(19.16, 34.87) * mm, "end": v(18.96, 36.47) * mm});
            skLineSegment(sketch, "E15.22.10", {"start": v(18.71, 36.8) * mm, "end": v(18.27, 37.06) * mm});
            skLineSegment(sketch, "E15.22.11", {"start": v(17.8, 37.25) * mm, "end": v(18.27, 37.06) * mm});
            skArc(sketch, "E15.22.12", {"start": v(18.94, 32.77) * mm, "mid": v(19.03, 33.01) * mm, "end": v(19.09, 33.27) * mm});
            skArc(sketch, "E15.22.13", {"start": v(17.8, 37.25) * mm, "mid": v(17.6, 37.29) * mm, "end": v(17.4, 37.24) * mm});
            skArc(sketch, "E15.22.14", {"start": v(14.77, 35.4) * mm, "mid": v(14.6, 35.2) * mm, "end": v(14.47, 34.97) * mm});
            skArc(sketch, "E15.22.15", {"start": v(18.96, 36.47) * mm, "mid": v(18.87, 36.66) * mm, "end": v(18.71, 36.8) * mm});
            skArc(sketch, "E15.23.0", {"start": v(9.52, 35.1) * mm, "mid": v(9.71, 33.98) * mm, "end": v(10.6, 33.28) * mm});
            skArc(sketch, "E15.23.1", {"start": v(2.94, 34.8) * mm, "mid": v(4.03, 35.11) * mm, "end": v(4.63, 36.07) * mm});
            skLineSegment(sketch, "E15.23.2", {"start": v(9.81, 36.55) * mm, "end": v(9.52, 35.1) * mm});
            skLineSegment(sketch, "E15.23.3", {"start": v(4.92, 37.53) * mm, "end": v(4.63, 36.07) * mm});
            skPoint(sketch, "E15.23.4", {"position": v(8.77, 40.33) * mm});
            skPoint(sketch, "E15.23.5", {"position": v(7.34, 40.62) * mm});
            skArc(sketch, "E15.23.6", {"start": v(5.1, 38.02) * mm, "mid": v(6.03, 39.33) * mm, "end": v(7.16, 40.47) * mm});
            skPoint(sketch, "E15.23.7", {"position": v(4.97, 37.77) * mm});
            skPoint(sketch, "E15.23.8", {"position": v(9.86, 36.8) * mm});
            skArc(sketch, "E15.23.9", {"start": v(9.83, 37.08) * mm, "mid": v(9.48, 38.64) * mm, "end": v(8.87, 40.13) * mm});
            skLineSegment(sketch, "E15.23.10", {"start": v(8.55, 40.4) * mm, "end": v(8.06, 40.52) * mm});
            skLineSegment(sketch, "E15.23.11", {"start": v(7.56, 40.59) * mm, "end": v(8.06, 40.52) * mm});
            skArc(sketch, "E15.23.12", {"start": v(9.81, 36.55) * mm, "mid": v(9.84, 36.81) * mm, "end": v(9.83, 37.08) * mm});
            skArc(sketch, "E15.23.13", {"start": v(7.56, 40.59) * mm, "mid": v(7.35, 40.57) * mm, "end": v(7.16, 40.47) * mm});
            skArc(sketch, "E15.23.14", {"start": v(5.1, 38.02) * mm, "mid": v(5, 37.78) * mm, "end": v(4.92, 37.53) * mm});
            skArc(sketch, "E15.23.15", {"start": v(8.87, 40.13) * mm, "mid": v(8.74, 40.3) * mm, "end": v(8.55, 40.4) * mm});
            skArc(sketch, "E16.trimOffspring", {"start": v(-14.85, 31.61) * mm, "mid": v(-15.45, 31.32) * mm, "end": v(-16.04, 31.03) * mm});
            skArc(sketch, "E17.trimOffspring", {"start": v(-22.53, 26.69) * mm, "mid": v(-23.03, 26.26) * mm, "end": v(-23.52, 25.82) * mm});
            skArc(sketch, "E18.trimOffspring", {"start": v(-28.67, 19.95) * mm, "mid": v(-29.04, 19.4) * mm, "end": v(-29.4, 18.85) * mm});
            skArc(sketch, "E19.trimOffspring", {"start": v(-32.85, 11.85) * mm, "mid": v(-33.07, 11.23) * mm, "end": v(-33.28, 10.6) * mm});
            skArc(sketch, "E20.trimOffspring", {"start": v(-34.8, 2.94) * mm, "mid": v(-34.85, 2.28) * mm, "end": v(-34.89, 1.62) * mm});
            skArc(sketch, "E21.trimOffspring", {"start": v(-34.38, -6.16) * mm, "mid": v(-34.25, -6.81) * mm, "end": v(-34.12, -7.46) * mm});
            skArc(sketch, "E22.trimOffspring", {"start": v(-31.61, -14.85) * mm, "mid": v(-31.32, -15.45) * mm, "end": v(-31.03, -16.04) * mm});
            skArc(sketch, "E23.trimOffspring", {"start": v(-26.69, -22.53) * mm, "mid": v(-26.26, -23.03) * mm, "end": v(-25.82, -23.52) * mm});
            skArc(sketch, "E24.trimOffspring", {"start": v(-19.95, -28.67) * mm, "mid": v(-19.4, -29.04) * mm, "end": v(-18.85, -29.4) * mm});
            skArc(sketch, "E25.trimOffspring", {"start": v(-11.85, -32.85) * mm, "mid": v(-11.23, -33.07) * mm, "end": v(-10.6, -33.28) * mm});
            skArc(sketch, "E26.trimOffspring", {"start": v(-2.94, -34.8) * mm, "mid": v(-2.28, -34.85) * mm, "end": v(-1.62, -34.89) * mm});
            skArc(sketch, "E27.trimOffspring", {"start": v(6.16, -34.38) * mm, "mid": v(6.81, -34.25) * mm, "end": v(7.46, -34.12) * mm});
            skArc(sketch, "E28.trimOffspring", {"start": v(14.85, -31.61) * mm, "mid": v(15.45, -31.32) * mm, "end": v(16.04, -31.03) * mm});
            skArc(sketch, "E29.trimOffspring", {"start": v(22.53, -26.69) * mm, "mid": v(23.03, -26.26) * mm, "end": v(23.52, -25.82) * mm});
            skArc(sketch, "E30.trimOffspring", {"start": v(28.67, -19.95) * mm, "mid": v(29.04, -19.4) * mm, "end": v(29.4, -18.85) * mm});
            skArc(sketch, "E31.trimOffspring", {"start": v(32.85, -11.85) * mm, "mid": v(33.07, -11.23) * mm, "end": v(33.28, -10.6) * mm});
            skArc(sketch, "E32.trimOffspring", {"start": v(34.8, -2.94) * mm, "mid": v(34.85, -2.28) * mm, "end": v(34.89, -1.62) * mm});
            skArc(sketch, "E33.trimOffspring", {"start": v(34.38, 6.16) * mm, "mid": v(34.25, 6.81) * mm, "end": v(34.12, 7.46) * mm});
            skArc(sketch, "E34.trimOffspring", {"start": v(31.61, 14.85) * mm, "mid": v(31.32, 15.45) * mm, "end": v(31.03, 16.04) * mm});
            skArc(sketch, "E35.trimOffspring", {"start": v(26.69, 22.53) * mm, "mid": v(26.26, 23.03) * mm, "end": v(25.82, 23.52) * mm});
            skArc(sketch, "E36.trimOffspring", {"start": v(19.95, 28.67) * mm, "mid": v(19.4, 29.04) * mm, "end": v(18.85, 29.4) * mm});
            skArc(sketch, "E37.trimOffspring", {"start": v(11.85, 32.85) * mm, "mid": v(11.23, 33.07) * mm, "end": v(10.6, 33.28) * mm});
            skArc(sketch, "E38.trimOffspring", {"start": v(2.94, 34.8) * mm, "mid": v(2.28, 34.85) * mm, "end": v(1.62, 34.89) * mm});
            skSolve(sketch);
        }
        {
            var Q0;
            Q0=qCreatedBy(makeId("Front.planeOp"),FACE);
            cPlane(context, id + "F1", {"entities" : qUnion([Q0]), "cplaneType" : CPlaneType.OFFSET, "offset" : 50.8 * mm, "width" : 152.4 * mm, "height" : 152.4 * mm});
        }
        {
            var Q0;
            Q0=qCreatedBy(id+"F1.planeOp",FACE);
            var sketch = newSketch(context, id + "F2", { "sketchPlane" : qUnion([Q0])});
            skArc(sketch, "E39", {"start": v(-6.14, 34.05) * mm, "mid": v(-6.8, 33.93) * mm, "end": v(-7.44, 33.8) * mm});
            skArc(sketch, "E40.trimOffspring", {"start": v(-0.08, 38.03) * mm, "mid": v(-0.82, 39.45) * mm, "end": v(-1.8, 40.73) * mm});
            skLineSegment(sketch, "E41", {"start": v(0.04, 37.52) * mm, "end": v(0.13, 36.04) * mm});
            skLineSegment(sketch, "E42", {"start": v(-2.17, 40.9) * mm, "end": v(-2.68, 40.9) * mm});
            skLineSegment(sketch, "E43.MirrorCS", {"start": v(-3.18, 40.83) * mm, "end": v(-2.68, 40.9) * mm});
            skArc(sketch, "E44.MirrorCS", {"start": v(-4.88, 37.71) * mm, "mid": v(-4.33, 39.22) * mm, "end": v(-3.54, 40.62) * mm});
            skLineSegment(sketch, "E45.MirrorCS", {"start": v(-4.94, 37.2) * mm, "end": v(-4.84, 35.72) * mm});
            skPoint(sketch, "E46.orphan", {"position": v(0.35, 32.78) * mm});
            skPoint(sketch, "E47.orphan", {"position": v(-4.62, 32.46) * mm});
            skPoint(sketch, "E48.visualSharp", {"position": v(0.23, 34.6) * mm});
            skArc(sketch, "E48.filletArc", {"start": v(0.13, 36.04) * mm, "mid": v(0.6, 35.01) * mm, "end": v(1.65, 34.56) * mm});
            skPoint(sketch, "E49.visualSharp", {"position": v(-4.74, 34.27) * mm});
            skArc(sketch, "E49.filletArc", {"start": v(-6.14, 34.05) * mm, "mid": v(-5.17, 34.63) * mm, "end": v(-4.84, 35.72) * mm});
            skPoint(sketch, "E50.visualSharp", {"position": v(-3.4, 40.8) * mm});
            skArc(sketch, "E50.filletArc", {"start": v(-3.18, 40.83) * mm, "mid": v(-3.38, 40.76) * mm, "end": v(-3.54, 40.62) * mm});
            skPoint(sketch, "E51.visualSharp", {"position": v(-1.95, 40.9) * mm});
            skArc(sketch, "E51.filletArc", {"start": v(-1.8, 40.73) * mm, "mid": v(-1.97, 40.86) * mm, "end": v(-2.17, 40.9) * mm});
            skPoint(sketch, "E52.visualSharp", {"position": v(-4.95, 37.45) * mm});
            skArc(sketch, "E52.filletArc", {"start": v(-4.88, 37.71) * mm, "mid": v(-4.93, 37.46) * mm, "end": v(-4.94, 37.2) * mm});
            skPoint(sketch, "E53.visualSharp", {"position": v(0.02, 37.77) * mm});
            skArc(sketch, "E53.filletArc", {"start": v(0.04, 37.52) * mm, "mid": v(0, 37.78) * mm, "end": v(-0.08, 38.03) * mm});
            skArc(sketch, "E54.1.0", {"start": v(-9.28, 34.83) * mm, "mid": v(-8.56, 33.96) * mm, "end": v(-7.44, 33.8) * mm});
            skArc(sketch, "E54.1.1", {"start": v(-14.83, 31.28) * mm, "mid": v(-14.04, 32.1) * mm, "end": v(-14, 33.23) * mm});
            skLineSegment(sketch, "E54.1.2", {"start": v(-9.76, 36.23) * mm, "end": v(-9.28, 34.83) * mm});
            skLineSegment(sketch, "E54.1.3", {"start": v(-14.48, 34.63) * mm, "end": v(-14, 33.23) * mm});
            skPoint(sketch, "E54.1.4", {"position": v(-12.55, 38.98) * mm});
            skPoint(sketch, "E54.1.5", {"position": v(-13.93, 38.52) * mm});
            skArc(sketch, "E54.1.6", {"start": v(-14.56, 35.15) * mm, "mid": v(-14.42, 36.75) * mm, "end": v(-14.01, 38.3) * mm});
            skPoint(sketch, "E54.1.7", {"position": v(-14.56, 34.87) * mm});
            skPoint(sketch, "E54.1.8", {"position": v(-9.84, 36.47) * mm});
            skArc(sketch, "E54.1.9", {"start": v(-10, 36.7) * mm, "mid": v(-11.1, 37.88) * mm, "end": v(-12.36, 38.86) * mm});
            skLineSegment(sketch, "E54.1.10", {"start": v(-12.77, 38.93) * mm, "end": v(-13.26, 38.8) * mm});
            skLineSegment(sketch, "E54.1.11", {"start": v(-13.73, 38.6) * mm, "end": v(-13.26, 38.8) * mm});
            skArc(sketch, "E54.1.12", {"start": v(-9.76, 36.23) * mm, "mid": v(-9.86, 36.48) * mm, "end": v(-10, 36.7) * mm});
            skArc(sketch, "E54.1.13", {"start": v(-13.73, 38.6) * mm, "mid": v(-13.9, 38.48) * mm, "end": v(-14.01, 38.3) * mm});
            skArc(sketch, "E54.1.14", {"start": v(-14.56, 35.15) * mm, "mid": v(-14.54, 34.89) * mm, "end": v(-14.48, 34.63) * mm});
            skArc(sketch, "E54.1.15", {"start": v(-12.36, 38.86) * mm, "mid": v(-12.56, 38.94) * mm, "end": v(-12.77, 38.93) * mm});
            skArc(sketch, "E54.2.0", {"start": v(-18.06, 31.23) * mm, "mid": v(-17.14, 30.57) * mm, "end": v(-16.02, 30.7) * mm});
            skArc(sketch, "E54.2.1", {"start": v(-22.5, 26.36) * mm, "mid": v(-21.96, 27.35) * mm, "end": v(-22.2, 28.46) * mm});
            skLineSegment(sketch, "E54.2.2", {"start": v(-18.89, 32.46) * mm, "end": v(-18.06, 31.23) * mm});
            skLineSegment(sketch, "E54.2.3", {"start": v(-23.03, 29.69) * mm, "end": v(-22.2, 28.46) * mm});
            skPoint(sketch, "E54.2.4", {"position": v(-22.3, 34.4) * mm});
            skPoint(sketch, "E54.2.5", {"position": v(-23.51, 33.58) * mm});
            skArc(sketch, "E54.2.6", {"start": v(-23.25, 30.17) * mm, "mid": v(-23.52, 31.75) * mm, "end": v(-23.53, 33.35) * mm});
            skPoint(sketch, "E54.2.7", {"position": v(-23.17, 29.9) * mm});
            skPoint(sketch, "E54.2.8", {"position": v(-19.03, 32.67) * mm});
            skArc(sketch, "E54.2.9", {"start": v(-19.25, 32.84) * mm, "mid": v(-20.6, 33.7) * mm, "end": v(-22.08, 34.32) * mm});
            skLineSegment(sketch, "E54.2.10", {"start": v(-22.5, 34.28) * mm, "end": v(-22.93, 34.03) * mm});
            skLineSegment(sketch, "E54.2.11", {"start": v(-23.34, 33.72) * mm, "end": v(-22.93, 34.03) * mm});
            skArc(sketch, "E54.2.12", {"start": v(-18.89, 32.46) * mm, "mid": v(-19.05, 32.66) * mm, "end": v(-19.25, 32.84) * mm});
            skArc(sketch, "E54.2.13", {"start": v(-23.34, 33.72) * mm, "mid": v(-23.47, 33.56) * mm, "end": v(-23.53, 33.35) * mm});
            skArc(sketch, "E54.2.14", {"start": v(-23.25, 30.17) * mm, "mid": v(-23.16, 29.92) * mm, "end": v(-23.03, 29.69) * mm});
            skArc(sketch, "E54.2.15", {"start": v(-22.08, 34.32) * mm, "mid": v(-22.3, 34.34) * mm, "end": v(-22.5, 34.28) * mm});
            skArc(sketch, "E54.3.0", {"start": v(-25.62, 25.47) * mm, "mid": v(-24.55, 25.08) * mm, "end": v(-23.5, 25.49) * mm});
            skArc(sketch, "E54.3.1", {"start": v(-28.64, 19.62) * mm, "mid": v(-28.37, 20.72) * mm, "end": v(-28.9, 21.72) * mm});
            skLineSegment(sketch, "E54.3.2", {"start": v(-26.73, 26.45) * mm, "end": v(-25.62, 25.47) * mm});
            skLineSegment(sketch, "E54.3.3", {"start": v(-30.02, 22.7) * mm, "end": v(-28.9, 21.72) * mm});
            skPoint(sketch, "E54.3.4", {"position": v(-30.53, 27.43) * mm});
            skPoint(sketch, "E54.3.5", {"position": v(-31.49, 26.33) * mm});
            skArc(sketch, "E54.3.6", {"start": v(-30.35, 23.1) * mm, "mid": v(-31.02, 24.56) * mm, "end": v(-31.45, 26.1) * mm});
            skPoint(sketch, "E54.3.7", {"position": v(-30.2, 22.87) * mm});
            skPoint(sketch, "E54.3.8", {"position": v(-26.92, 26.61) * mm});
            skArc(sketch, "E54.3.9", {"start": v(-27.17, 26.72) * mm, "mid": v(-28.7, 27.2) * mm, "end": v(-30.3, 27.42) * mm});
            skLineSegment(sketch, "E54.3.10", {"start": v(-30.68, 27.27) * mm, "end": v(-31.04, 26.91) * mm});
            skLineSegment(sketch, "E54.3.11", {"start": v(-31.35, 26.51) * mm, "end": v(-31.04, 26.91) * mm});
            skArc(sketch, "E54.3.12", {"start": v(-26.73, 26.45) * mm, "mid": v(-26.94, 26.6) * mm, "end": v(-27.17, 26.72) * mm});
            skArc(sketch, "E54.3.13", {"start": v(-31.35, 26.51) * mm, "mid": v(-31.44, 26.32) * mm, "end": v(-31.45, 26.1) * mm});
            skArc(sketch, "E54.3.14", {"start": v(-30.35, 23.1) * mm, "mid": v(-30.2, 22.89) * mm, "end": v(-30.02, 22.7) * mm});
            skArc(sketch, "E54.3.15", {"start": v(-30.3, 27.42) * mm, "mid": v(-30.5, 27.39) * mm, "end": v(-30.68, 27.27) * mm});
            skArc(sketch, "E54.4.0", {"start": v(-31.42, 17.95) * mm, "mid": v(-30.3, 17.85) * mm, "end": v(-29.38, 18.52) * mm});
            skArc(sketch, "E54.4.1", {"start": v(-32.83, 11.52) * mm, "mid": v(-32.85, 12.65) * mm, "end": v(-33.62, 13.49) * mm});
            skLineSegment(sketch, "E54.4.2", {"start": v(-32.75, 18.61) * mm, "end": v(-31.42, 17.95) * mm});
            skLineSegment(sketch, "E54.4.3", {"start": v(-34.95, 14.14) * mm, "end": v(-33.62, 13.49) * mm});
            skPoint(sketch, "E54.4.4", {"position": v(-36.67, 18.58) * mm});
            skPoint(sketch, "E54.4.5", {"position": v(-37.31, 17.27) * mm});
            skArc(sketch, "E54.4.6", {"start": v(-35.38, 14.45) * mm, "mid": v(-36.4, 15.68) * mm, "end": v(-37.22, 17.06) * mm});
            skPoint(sketch, "E54.4.7", {"position": v(-35.18, 14.25) * mm});
            skPoint(sketch, "E54.4.8", {"position": v(-32.97, 18.72) * mm});
            skArc(sketch, "E54.4.9", {"start": v(-33.25, 18.76) * mm, "mid": v(-34.85, 18.83) * mm, "end": v(-36.45, 18.63) * mm});
            skLineSegment(sketch, "E54.4.10", {"start": v(-36.78, 18.39) * mm, "end": v(-37.03, 17.95) * mm});
            skLineSegment(sketch, "E54.4.11", {"start": v(-37.23, 17.48) * mm, "end": v(-37.03, 17.95) * mm});
            skArc(sketch, "E54.4.12", {"start": v(-32.75, 18.61) * mm, "mid": v(-33, 18.7) * mm, "end": v(-33.25, 18.76) * mm});
            skArc(sketch, "E54.4.13", {"start": v(-37.23, 17.48) * mm, "mid": v(-37.27, 17.27) * mm, "end": v(-37.22, 17.06) * mm});
            skArc(sketch, "E54.4.14", {"start": v(-35.38, 14.45) * mm, "mid": v(-35.18, 14.28) * mm, "end": v(-34.95, 14.14) * mm});
            skArc(sketch, "E54.4.15", {"start": v(-36.45, 18.63) * mm, "mid": v(-36.64, 18.54) * mm, "end": v(-36.78, 18.39) * mm});
            skArc(sketch, "E54.5.0", {"start": v(-35.08, 9.2) * mm, "mid": v(-33.96, 9.38) * mm, "end": v(-33.26, 10.27) * mm});
            skArc(sketch, "E54.5.1", {"start": v(-34.78, 2.62) * mm, "mid": v(-35.1, 3.7) * mm, "end": v(-36.05, 4.3) * mm});
            skLineSegment(sketch, "E54.5.2", {"start": v(-36.53, 9.48) * mm, "end": v(-35.08, 9.2) * mm});
            skLineSegment(sketch, "E54.5.3", {"start": v(-37.5, 4.6) * mm, "end": v(-36.05, 4.3) * mm});
            skPoint(sketch, "E54.5.4", {"position": v(-40.31, 8.44) * mm});
            skPoint(sketch, "E54.5.5", {"position": v(-40.6, 7) * mm});
            skArc(sketch, "E54.5.6", {"start": v(-38, 4.78) * mm, "mid": v(-39.3, 5.7) * mm, "end": v(-40.45, 6.83) * mm});
            skPoint(sketch, "E54.5.7", {"position": v(-37.75, 4.65) * mm});
            skPoint(sketch, "E54.5.8", {"position": v(-36.78, 9.53) * mm});
            skArc(sketch, "E54.5.9", {"start": v(-37.05, 9.5) * mm, "mid": v(-38.62, 9.15) * mm, "end": v(-40.1, 8.54) * mm});
            skLineSegment(sketch, "E54.5.10", {"start": v(-40.37, 8.22) * mm, "end": v(-40.5, 7.73) * mm});
            skLineSegment(sketch, "E54.5.11", {"start": v(-40.57, 7.23) * mm, "end": v(-40.5, 7.73) * mm});
            skArc(sketch, "E54.5.12", {"start": v(-36.53, 9.48) * mm, "mid": v(-36.8, 9.51) * mm, "end": v(-37.05, 9.5) * mm});
            skArc(sketch, "E54.5.13", {"start": v(-40.57, 7.23) * mm, "mid": v(-40.55, 7.02) * mm, "end": v(-40.45, 6.83) * mm});
            skArc(sketch, "E54.5.14", {"start": v(-38, 4.78) * mm, "mid": v(-37.76, 4.67) * mm, "end": v(-37.5, 4.6) * mm});
            skArc(sketch, "E54.5.15", {"start": v(-40.1, 8.54) * mm, "mid": v(-40.27, 8.41) * mm, "end": v(-40.37, 8.22) * mm});
            skArc(sketch, "E54.6.0", {"start": v(-36.35, -0.21) * mm, "mid": v(-35.32, 0.26) * mm, "end": v(-34.87, 1.3) * mm});
            skArc(sketch, "E54.6.1", {"start": v(-34.36, -6.5) * mm, "mid": v(-34.94, -5.52) * mm, "end": v(-36.02, -5.19) * mm});
            skLineSegment(sketch, "E54.6.2", {"start": v(-37.83, -0.31) * mm, "end": v(-36.35, -0.21) * mm});
            skLineSegment(sketch, "E54.6.3", {"start": v(-37.5, -5.28) * mm, "end": v(-36.02, -5.19) * mm});
            skPoint(sketch, "E54.6.4", {"position": v(-41.2, -2.3) * mm});
            skPoint(sketch, "E54.6.5", {"position": v(-41.11, -3.75) * mm});
            skArc(sketch, "E54.6.6", {"start": v(-38.02, -5.23) * mm, "mid": v(-39.53, -4.68) * mm, "end": v(-40.92, -3.89) * mm});
            skPoint(sketch, "E54.6.7", {"position": v(-37.75, -5.3) * mm});
            skPoint(sketch, "E54.6.8", {"position": v(-38.08, -0.33) * mm});
            skArc(sketch, "E54.6.9", {"start": v(-38.34, -0.43) * mm, "mid": v(-39.76, -1.17) * mm, "end": v(-41.04, -2.14) * mm});
            skLineSegment(sketch, "E54.6.10", {"start": v(-41.2, -2.52) * mm, "end": v(-41.2, -3.03) * mm});
            skLineSegment(sketch, "E54.6.11", {"start": v(-41.14, -3.53) * mm, "end": v(-41.2, -3.03) * mm});
            skArc(sketch, "E54.6.12", {"start": v(-37.83, -0.31) * mm, "mid": v(-38.09, -0.35) * mm, "end": v(-38.34, -0.43) * mm});
            skArc(sketch, "E54.6.13", {"start": v(-41.14, -3.53) * mm, "mid": v(-41.07, -3.73) * mm, "end": v(-40.92, -3.89) * mm});
            skArc(sketch, "E54.6.14", {"start": v(-38.02, -5.23) * mm, "mid": v(-37.76, -5.28) * mm, "end": v(-37.5, -5.28) * mm});
            skArc(sketch, "E54.6.15", {"start": v(-41.04, -2.14) * mm, "mid": v(-41.16, -2.32) * mm, "end": v(-41.2, -2.52) * mm});
            skArc(sketch, "E54.7.0", {"start": v(-35.14, -9.63) * mm, "mid": v(-34.27, -8.9) * mm, "end": v(-34.1, -7.79) * mm});
            skArc(sketch, "E54.7.1", {"start": v(-31.59, -15.18) * mm, "mid": v(-32.4, -14.4) * mm, "end": v(-33.54, -14.35) * mm});
            skLineSegment(sketch, "E54.7.2", {"start": v(-36.54, -10.1) * mm, "end": v(-35.14, -9.63) * mm});
            skLineSegment(sketch, "E54.7.3", {"start": v(-34.94, -14.83) * mm, "end": v(-33.54, -14.35) * mm});
            skPoint(sketch, "E54.7.4", {"position": v(-39.3, -12.9) * mm});
            skPoint(sketch, "E54.7.5", {"position": v(-38.82, -14.28) * mm});
            skArc(sketch, "E54.7.6", {"start": v(-35.45, -14.91) * mm, "mid": v(-37.05, -14.77) * mm, "end": v(-38.6, -14.36) * mm});
            skPoint(sketch, "E54.7.7", {"position": v(-35.18, -14.9) * mm});
            skPoint(sketch, "E54.7.8", {"position": v(-36.78, -10.19) * mm});
            skArc(sketch, "E54.7.9", {"start": v(-37, -10.35) * mm, "mid": v(-38.19, -11.44) * mm, "end": v(-39.17, -12.7) * mm});
            skLineSegment(sketch, "E54.7.10", {"start": v(-39.23, -13.12) * mm, "end": v(-39.1, -13.6) * mm});
            skLineSegment(sketch, "E54.7.11", {"start": v(-38.9, -14.08) * mm, "end": v(-39.1, -13.6) * mm});
            skArc(sketch, "E54.7.12", {"start": v(-36.54, -10.1) * mm, "mid": v(-36.78, -10.21) * mm, "end": v(-37, -10.35) * mm});
            skArc(sketch, "E54.7.13", {"start": v(-38.9, -14.08) * mm, "mid": v(-38.79, -14.25) * mm, "end": v(-38.6, -14.36) * mm});
            skArc(sketch, "E54.7.14", {"start": v(-35.45, -14.91) * mm, "mid": v(-35.2, -14.9) * mm, "end": v(-34.94, -14.83) * mm});
            skArc(sketch, "E54.7.15", {"start": v(-39.17, -12.7) * mm, "mid": v(-39.24, -12.9) * mm, "end": v(-39.23, -13.12) * mm});
            skArc(sketch, "E54.8.0", {"start": v(-31.53, -18.41) * mm, "mid": v(-30.88, -17.5) * mm, "end": v(-31, -16.37) * mm});
            skArc(sketch, "E54.8.1", {"start": v(-26.67, -22.85) * mm, "mid": v(-27.66, -22.3) * mm, "end": v(-28.76, -22.56) * mm});
            skLineSegment(sketch, "E54.8.2", {"start": v(-32.76, -19.24) * mm, "end": v(-31.53, -18.41) * mm});
            skLineSegment(sketch, "E54.8.3", {"start": v(-30, -23.38) * mm, "end": v(-28.76, -22.56) * mm});
            skPoint(sketch, "E54.8.4", {"position": v(-34.7, -22.65) * mm});
            skPoint(sketch, "E54.8.5", {"position": v(-33.89, -23.86) * mm});
            skArc(sketch, "E54.8.6", {"start": v(-30.47, -23.6) * mm, "mid": v(-32.05, -23.87) * mm, "end": v(-33.66, -23.88) * mm});
            skPoint(sketch, "E54.8.7", {"position": v(-30.2, -23.52) * mm});
            skPoint(sketch, "E54.8.8", {"position": v(-32.97, -19.38) * mm});
            skArc(sketch, "E54.8.9", {"start": v(-33.14, -19.6) * mm, "mid": v(-34, -20.95) * mm, "end": v(-34.63, -22.43) * mm});
            skLineSegment(sketch, "E54.8.10", {"start": v(-34.59, -22.84) * mm, "end": v(-34.33, -23.28) * mm});
            skLineSegment(sketch, "E54.8.11", {"start": v(-34.02, -23.69) * mm, "end": v(-34.33, -23.28) * mm});
            skArc(sketch, "E54.8.12", {"start": v(-32.76, -19.24) * mm, "mid": v(-32.97, -19.4) * mm, "end": v(-33.14, -19.6) * mm});
            skArc(sketch, "E54.8.13", {"start": v(-34.02, -23.69) * mm, "mid": v(-33.86, -23.82) * mm, "end": v(-33.66, -23.88) * mm});
            skArc(sketch, "E54.8.14", {"start": v(-30.47, -23.6) * mm, "mid": v(-30.22, -23.5) * mm, "end": v(-30, -23.38) * mm});
            skArc(sketch, "E54.8.15", {"start": v(-34.63, -22.43) * mm, "mid": v(-34.65, -22.64) * mm, "end": v(-34.59, -22.84) * mm});
            skArc(sketch, "E54.9.0", {"start": v(-25.78, -25.96) * mm, "mid": v(-25.38, -24.9) * mm, "end": v(-25.8, -23.85) * mm});
            skArc(sketch, "E54.9.1", {"start": v(-19.93, -29) * mm, "mid": v(-21.03, -28.72) * mm, "end": v(-22.03, -29.25) * mm});
            skLineSegment(sketch, "E54.9.2", {"start": v(-26.75, -27.08) * mm, "end": v(-25.78, -25.96) * mm});
            skLineSegment(sketch, "E54.9.3", {"start": v(-23, -30.36) * mm, "end": v(-22.03, -29.25) * mm});
            skPoint(sketch, "E54.9.4", {"position": v(-27.74, -30.87) * mm});
            skPoint(sketch, "E54.9.5", {"position": v(-26.64, -31.84) * mm});
            skArc(sketch, "E54.9.6", {"start": v(-23.41, -30.7) * mm, "mid": v(-24.87, -31.37) * mm, "end": v(-26.42, -31.8) * mm});
            skPoint(sketch, "E54.9.7", {"position": v(-23.17, -30.55) * mm});
            skPoint(sketch, "E54.9.8", {"position": v(-26.92, -27.27) * mm});
            skArc(sketch, "E54.9.9", {"start": v(-27.03, -27.52) * mm, "mid": v(-27.5, -29.06) * mm, "end": v(-27.73, -30.65) * mm});
            skLineSegment(sketch, "E54.9.10", {"start": v(-27.58, -31.03) * mm, "end": v(-27.22, -31.4) * mm});
            skLineSegment(sketch, "E54.9.11", {"start": v(-26.82, -31.7) * mm, "end": v(-27.22, -31.4) * mm});
            skArc(sketch, "E54.9.12", {"start": v(-26.75, -27.08) * mm, "mid": v(-26.9, -27.29) * mm, "end": v(-27.03, -27.52) * mm});
            skArc(sketch, "E54.9.13", {"start": v(-26.82, -31.7) * mm, "mid": v(-26.63, -31.8) * mm, "end": v(-26.42, -31.8) * mm});
            skArc(sketch, "E54.9.14", {"start": v(-23.41, -30.7) * mm, "mid": v(-23.2, -30.55) * mm, "end": v(-23, -30.36) * mm});
            skArc(sketch, "E54.9.15", {"start": v(-27.73, -30.65) * mm, "mid": v(-27.7, -30.85) * mm, "end": v(-27.58, -31.03) * mm});
            skArc(sketch, "E54.10.0", {"start": v(-18.26, -31.77) * mm, "mid": v(-18.16, -30.64) * mm, "end": v(-18.83, -29.73) * mm});
            skArc(sketch, "E54.10.1", {"start": v(-11.83, -33.18) * mm, "mid": v(-12.96, -33.2) * mm, "end": v(-13.8, -33.97) * mm});
            skLineSegment(sketch, "E54.10.2", {"start": v(-18.92, -33.1) * mm, "end": v(-18.26, -31.77) * mm});
            skLineSegment(sketch, "E54.10.3", {"start": v(-14.45, -35.3) * mm, "end": v(-13.8, -33.97) * mm});
            skPoint(sketch, "E54.10.4", {"position": v(-18.88, -37.02) * mm});
            skPoint(sketch, "E54.10.5", {"position": v(-17.58, -37.66) * mm});
            skArc(sketch, "E54.10.6", {"start": v(-14.75, -35.73) * mm, "mid": v(-15.98, -36.76) * mm, "end": v(-17.37, -37.57) * mm});
            skPoint(sketch, "E54.10.7", {"position": v(-14.56, -35.53) * mm});
            skPoint(sketch, "E54.10.8", {"position": v(-19.03, -33.32) * mm});
            skArc(sketch, "E54.10.9", {"start": v(-19.07, -33.6) * mm, "mid": v(-19.14, -35.2) * mm, "end": v(-18.94, -36.8) * mm});
            skLineSegment(sketch, "E54.10.10", {"start": v(-18.7, -37.13) * mm, "end": v(-18.25, -37.38) * mm});
            skLineSegment(sketch, "E54.10.11", {"start": v(-17.78, -37.58) * mm, "end": v(-18.25, -37.38) * mm});
            skArc(sketch, "E54.10.12", {"start": v(-18.92, -33.1) * mm, "mid": v(-19.01, -33.34) * mm, "end": v(-19.07, -33.6) * mm});
            skArc(sketch, "E54.10.13", {"start": v(-17.78, -37.58) * mm, "mid": v(-17.58, -37.62) * mm, "end": v(-17.37, -37.57) * mm});
            skArc(sketch, "E54.10.14", {"start": v(-14.75, -35.73) * mm, "mid": v(-14.58, -35.53) * mm, "end": v(-14.45, -35.3) * mm});
            skArc(sketch, "E54.10.15", {"start": v(-18.94, -36.8) * mm, "mid": v(-18.85, -36.99) * mm, "end": v(-18.7, -37.13) * mm});
            skArc(sketch, "E54.11.0", {"start": v(-9.5, -35.43) * mm, "mid": v(-9.7, -34.31) * mm, "end": v(-10.58, -33.6) * mm});
            skArc(sketch, "E54.11.1", {"start": v(-2.92, -35.13) * mm, "mid": v(-4.01, -35.44) * mm, "end": v(-4.61, -36.4) * mm});
            skLineSegment(sketch, "E54.11.2", {"start": v(-9.8, -36.88) * mm, "end": v(-9.5, -35.43) * mm});
            skLineSegment(sketch, "E54.11.3", {"start": v(-4.9, -37.85) * mm, "end": v(-4.61, -36.4) * mm});
            skPoint(sketch, "E54.11.4", {"position": v(-8.74, -40.66) * mm});
            skPoint(sketch, "E54.11.5", {"position": v(-7.31, -40.95) * mm});
            skArc(sketch, "E54.11.6", {"start": v(-5.09, -38.34) * mm, "mid": v(-6, -39.66) * mm, "end": v(-7.14, -40.8) * mm});
            skPoint(sketch, "E54.11.7", {"position": v(-4.95, -38.1) * mm});
            skPoint(sketch, "E54.11.8", {"position": v(-9.84, -37.13) * mm});
            skArc(sketch, "E54.11.9", {"start": v(-9.8, -37.4) * mm, "mid": v(-9.46, -38.97) * mm, "end": v(-8.85, -40.46) * mm});
            skLineSegment(sketch, "E54.11.10", {"start": v(-8.53, -40.72) * mm, "end": v(-8.04, -40.85) * mm});
            skLineSegment(sketch, "E54.11.11", {"start": v(-7.54, -40.92) * mm, "end": v(-8.04, -40.85) * mm});
            skArc(sketch, "E54.11.12", {"start": v(-9.8, -36.88) * mm, "mid": v(-9.82, -37.14) * mm, "end": v(-9.8, -37.4) * mm});
            skArc(sketch, "E54.11.13", {"start": v(-7.54, -40.92) * mm, "mid": v(-7.32, -40.9) * mm, "end": v(-7.14, -40.8) * mm});
            skArc(sketch, "E54.11.14", {"start": v(-5.09, -38.34) * mm, "mid": v(-4.97, -38.1) * mm, "end": v(-4.9, -37.85) * mm});
            skArc(sketch, "E54.11.15", {"start": v(-8.85, -40.46) * mm, "mid": v(-8.72, -40.62) * mm, "end": v(-8.53, -40.72) * mm});
            skArc(sketch, "E54.12.0", {"start": v(-0.1, -36.7) * mm, "mid": v(-0.56, -35.67) * mm, "end": v(-1.6, -35.22) * mm});
            skArc(sketch, "E54.12.1", {"start": v(6.19, -34.7) * mm, "mid": v(5.21, -35.29) * mm, "end": v(4.88, -36.37) * mm});
            skLineSegment(sketch, "E54.12.2", {"start": v(0, -38.18) * mm, "end": v(-0.1, -36.7) * mm});
            skLineSegment(sketch, "E54.12.3", {"start": v(4.98, -37.85) * mm, "end": v(4.88, -36.37) * mm});
            skPoint(sketch, "E54.12.4", {"position": v(2, -41.56) * mm});
            skPoint(sketch, "E54.12.5", {"position": v(3.45, -41.46) * mm});
            skArc(sketch, "E54.12.6", {"start": v(4.93, -38.37) * mm, "mid": v(4.38, -39.88) * mm, "end": v(3.58, -41.27) * mm});
            skPoint(sketch, "E54.12.7", {"position": v(5, -38.1) * mm});
            skPoint(sketch, "E54.12.8", {"position": v(0.02, -38.43) * mm});
            skArc(sketch, "E54.12.9", {"start": v(0.12, -38.68) * mm, "mid": v(0.87, -40.1) * mm, "end": v(1.84, -41.39) * mm});
            skLineSegment(sketch, "E54.12.10", {"start": v(2.22, -41.56) * mm, "end": v(2.72, -41.56) * mm});
            skLineSegment(sketch, "E54.12.11", {"start": v(3.23, -41.49) * mm, "end": v(2.72, -41.56) * mm});
            skArc(sketch, "E54.12.12", {"start": v(0, -38.18) * mm, "mid": v(0.04, -38.44) * mm, "end": v(0.12, -38.68) * mm});
            skArc(sketch, "E54.12.13", {"start": v(3.23, -41.49) * mm, "mid": v(3.43, -41.42) * mm, "end": v(3.58, -41.27) * mm});
            skArc(sketch, "E54.12.14", {"start": v(4.93, -38.37) * mm, "mid": v(4.97, -38.11) * mm, "end": v(4.98, -37.85) * mm});
            skArc(sketch, "E54.12.15", {"start": v(1.84, -41.39) * mm, "mid": v(2, -41.51) * mm, "end": v(2.22, -41.56) * mm});
            skArc(sketch, "E54.13.0", {"start": v(9.32, -35.49) * mm, "mid": v(8.6, -34.62) * mm, "end": v(7.48, -34.45) * mm});
            skArc(sketch, "E54.13.1", {"start": v(14.87, -31.94) * mm, "mid": v(14.09, -32.75) * mm, "end": v(14.04, -33.89) * mm});
            skLineSegment(sketch, "E54.13.2", {"start": v(9.8, -36.9) * mm, "end": v(9.32, -35.49) * mm});
            skLineSegment(sketch, "E54.13.3", {"start": v(14.52, -35.29) * mm, "end": v(14.04, -33.89) * mm});
            skPoint(sketch, "E54.13.4", {"position": v(12.6, -39.64) * mm});
            skPoint(sketch, "E54.13.5", {"position": v(13.98, -39.17) * mm});
            skArc(sketch, "E54.13.6", {"start": v(14.6, -35.8) * mm, "mid": v(14.46, -37.4) * mm, "end": v(14.06, -38.96) * mm});
            skPoint(sketch, "E54.13.7", {"position": v(14.6, -35.53) * mm});
            skPoint(sketch, "E54.13.8", {"position": v(9.88, -37.13) * mm});
            skArc(sketch, "E54.13.9", {"start": v(10.05, -37.35) * mm, "mid": v(11.13, -38.53) * mm, "end": v(12.4, -39.52) * mm});
            skLineSegment(sketch, "E54.13.10", {"start": v(12.81, -39.58) * mm, "end": v(13.3, -39.45) * mm});
            skLineSegment(sketch, "E54.13.11", {"start": v(13.77, -39.26) * mm, "end": v(13.3, -39.45) * mm});
            skArc(sketch, "E54.13.12", {"start": v(9.8, -36.9) * mm, "mid": v(9.9, -37.13) * mm, "end": v(10.05, -37.35) * mm});
            skArc(sketch, "E54.13.13", {"start": v(13.77, -39.26) * mm, "mid": v(13.95, -39.14) * mm, "end": v(14.06, -38.96) * mm});
            skArc(sketch, "E54.13.14", {"start": v(14.6, -35.8) * mm, "mid": v(14.58, -35.54) * mm, "end": v(14.52, -35.29) * mm});
            skArc(sketch, "E54.13.15", {"start": v(12.4, -39.52) * mm, "mid": v(12.6, -39.6) * mm, "end": v(12.81, -39.58) * mm});
            skArc(sketch, "E54.14.0", {"start": v(18.1, -31.88) * mm, "mid": v(17.18, -31.23) * mm, "end": v(16.06, -31.35) * mm});
            skArc(sketch, "E54.14.1", {"start": v(22.55, -27.02) * mm, "mid": v(22, -28) * mm, "end": v(22.25, -29.11) * mm});
            skLineSegment(sketch, "E54.14.2", {"start": v(18.93, -33.11) * mm, "end": v(18.1, -31.88) * mm});
            skLineSegment(sketch, "E54.14.3", {"start": v(23.07, -30.34) * mm, "end": v(22.25, -29.11) * mm});
            skPoint(sketch, "E54.14.4", {"position": v(22.34, -35.05) * mm});
            skPoint(sketch, "E54.14.5", {"position": v(23.56, -34.24) * mm});
            skArc(sketch, "E54.14.6", {"start": v(23.29, -30.82) * mm, "mid": v(23.57, -32.4) * mm, "end": v(23.58, -34) * mm});
            skPoint(sketch, "E54.14.7", {"position": v(23.22, -30.55) * mm});
            skPoint(sketch, "E54.14.8", {"position": v(19.07, -33.32) * mm});
            skArc(sketch, "E54.14.9", {"start": v(19.29, -33.5) * mm, "mid": v(20.64, -34.36) * mm, "end": v(22.12, -34.98) * mm});
            skLineSegment(sketch, "E54.14.10", {"start": v(22.54, -34.94) * mm, "end": v(22.98, -34.68) * mm});
            skLineSegment(sketch, "E54.14.11", {"start": v(23.38, -34.37) * mm, "end": v(22.98, -34.68) * mm});
            skArc(sketch, "E54.14.12", {"start": v(18.93, -33.11) * mm, "mid": v(19.1, -33.32) * mm, "end": v(19.29, -33.5) * mm});
            skArc(sketch, "E54.14.13", {"start": v(23.38, -34.37) * mm, "mid": v(23.52, -34.21) * mm, "end": v(23.58, -34) * mm});
            skArc(sketch, "E54.14.14", {"start": v(23.29, -30.82) * mm, "mid": v(23.2, -30.57) * mm, "end": v(23.07, -30.34) * mm});
            skArc(sketch, "E54.14.15", {"start": v(22.12, -34.98) * mm, "mid": v(22.33, -35) * mm, "end": v(22.54, -34.94) * mm});
            skArc(sketch, "E54.15.0", {"start": v(25.66, -26.13) * mm, "mid": v(24.6, -25.73) * mm, "end": v(23.54, -26.15) * mm});
            skArc(sketch, "E54.15.1", {"start": v(28.69, -20.28) * mm, "mid": v(28.42, -21.38) * mm, "end": v(28.94, -22.38) * mm});
            skLineSegment(sketch, "E54.15.2", {"start": v(26.77, -27.1) * mm, "end": v(25.66, -26.13) * mm});
            skLineSegment(sketch, "E54.15.3", {"start": v(30.06, -23.36) * mm, "end": v(28.94, -22.38) * mm});
            skPoint(sketch, "E54.15.4", {"position": v(30.57, -28.09) * mm});
            skPoint(sketch, "E54.15.5", {"position": v(31.53, -27) * mm});
            skArc(sketch, "E54.15.6", {"start": v(30.39, -23.76) * mm, "mid": v(31.07, -25.22) * mm, "end": v(31.5, -26.77) * mm});
            skPoint(sketch, "E54.15.7", {"position": v(30.25, -23.52) * mm});
            skPoint(sketch, "E54.15.8", {"position": v(26.96, -27.27) * mm});
            skArc(sketch, "E54.15.9", {"start": v(27.22, -27.38) * mm, "mid": v(28.75, -27.86) * mm, "end": v(30.34, -28.08) * mm});
            skLineSegment(sketch, "E54.15.10", {"start": v(30.73, -27.93) * mm, "end": v(31.08, -27.57) * mm});
            skLineSegment(sketch, "E54.15.11", {"start": v(31.4, -27.17) * mm, "end": v(31.08, -27.57) * mm});
            skArc(sketch, "E54.15.12", {"start": v(26.77, -27.1) * mm, "mid": v(26.98, -27.26) * mm, "end": v(27.22, -27.38) * mm});
            skArc(sketch, "E54.15.13", {"start": v(31.4, -27.17) * mm, "mid": v(31.48, -26.98) * mm, "end": v(31.5, -26.77) * mm});
            skArc(sketch, "E54.15.14", {"start": v(30.39, -23.76) * mm, "mid": v(30.24, -23.54) * mm, "end": v(30.06, -23.36) * mm});
            skArc(sketch, "E54.15.15", {"start": v(30.34, -28.08) * mm, "mid": v(30.55, -28.04) * mm, "end": v(30.73, -27.93) * mm});
            skArc(sketch, "E54.16.0", {"start": v(31.46, -18.61) * mm, "mid": v(30.33, -18.5) * mm, "end": v(29.42, -19.18) * mm});
            skArc(sketch, "E54.16.1", {"start": v(32.87, -12.18) * mm, "mid": v(32.9, -13.31) * mm, "end": v(33.67, -14.14) * mm});
            skLineSegment(sketch, "E54.16.2", {"start": v(32.8, -19.27) * mm, "end": v(31.46, -18.61) * mm});
            skLineSegment(sketch, "E54.16.3", {"start": v(35, -14.8) * mm, "end": v(33.67, -14.14) * mm});
            skPoint(sketch, "E54.16.4", {"position": v(36.71, -19.23) * mm});
            skPoint(sketch, "E54.16.5", {"position": v(37.36, -17.93) * mm});
            skArc(sketch, "E54.16.6", {"start": v(35.42, -15.1) * mm, "mid": v(36.45, -16.33) * mm, "end": v(37.26, -17.72) * mm});
            skPoint(sketch, "E54.16.7", {"position": v(35.22, -14.9) * mm});
            skPoint(sketch, "E54.16.8", {"position": v(33.02, -19.38) * mm});
            skArc(sketch, "E54.16.9", {"start": v(33.3, -19.42) * mm, "mid": v(34.9, -19.49) * mm, "end": v(36.49, -19.28) * mm});
            skLineSegment(sketch, "E54.16.10", {"start": v(36.82, -19.04) * mm, "end": v(37.08, -18.6) * mm});
            skLineSegment(sketch, "E54.16.11", {"start": v(37.27, -18.13) * mm, "end": v(37.08, -18.6) * mm});
            skArc(sketch, "E54.16.12", {"start": v(32.8, -19.27) * mm, "mid": v(33.03, -19.36) * mm, "end": v(33.3, -19.42) * mm});
            skArc(sketch, "E54.16.13", {"start": v(37.27, -18.13) * mm, "mid": v(37.3, -17.92) * mm, "end": v(37.26, -17.72) * mm});
            skArc(sketch, "E54.16.14", {"start": v(35.42, -15.1) * mm, "mid": v(35.22, -14.93) * mm, "end": v(35, -14.8) * mm});
            skArc(sketch, "E54.16.15", {"start": v(36.49, -19.28) * mm, "mid": v(36.68, -19.2) * mm, "end": v(36.82, -19.04) * mm});
            skArc(sketch, "E54.17.0", {"start": v(35.12, -9.85) * mm, "mid": v(34, -10.04) * mm, "end": v(33.3, -10.93) * mm});
            skArc(sketch, "E54.17.1", {"start": v(34.82, -3.27) * mm, "mid": v(35.14, -4.36) * mm, "end": v(36.1, -4.96) * mm});
            skLineSegment(sketch, "E54.17.2", {"start": v(36.58, -10.14) * mm, "end": v(35.12, -9.85) * mm});
            skLineSegment(sketch, "E54.17.3", {"start": v(37.55, -5.25) * mm, "end": v(36.1, -4.96) * mm});
            skPoint(sketch, "E54.17.4", {"position": v(40.35, -9.1) * mm});
            skPoint(sketch, "E54.17.5", {"position": v(40.64, -7.66) * mm});
            skArc(sketch, "E54.17.6", {"start": v(38.04, -5.44) * mm, "mid": v(39.35, -6.36) * mm, "end": v(40.5, -7.49) * mm});
            skPoint(sketch, "E54.17.7", {"position": v(37.8, -5.3) * mm});
            skPoint(sketch, "E54.17.8", {"position": v(36.82, -10.19) * mm});
            skArc(sketch, "E54.17.9", {"start": v(37.1, -10.16) * mm, "mid": v(38.67, -9.8) * mm, "end": v(40.15, -9.2) * mm});
            skLineSegment(sketch, "E54.17.10", {"start": v(40.41, -8.88) * mm, "end": v(40.54, -8.39) * mm});
            skLineSegment(sketch, "E54.17.11", {"start": v(40.61, -7.88) * mm, "end": v(40.54, -8.39) * mm});
            skArc(sketch, "E54.17.12", {"start": v(36.58, -10.14) * mm, "mid": v(36.84, -10.17) * mm, "end": v(37.1, -10.16) * mm});
            skArc(sketch, "E54.17.13", {"start": v(40.61, -7.88) * mm, "mid": v(40.6, -7.67) * mm, "end": v(40.5, -7.49) * mm});
            skArc(sketch, "E54.17.14", {"start": v(38.04, -5.44) * mm, "mid": v(37.8, -5.32) * mm, "end": v(37.55, -5.25) * mm});
            skArc(sketch, "E54.17.15", {"start": v(40.15, -9.2) * mm, "mid": v(40.32, -9.07) * mm, "end": v(40.41, -8.88) * mm});
            skArc(sketch, "E54.18.0", {"start": v(36.4, -0.44) * mm, "mid": v(35.36, -0.91) * mm, "end": v(34.9, -1.95) * mm});
            skArc(sketch, "E54.18.1", {"start": v(34.4, 5.84) * mm, "mid": v(34.98, 4.87) * mm, "end": v(36.06, 4.53) * mm});
            skLineSegment(sketch, "E54.18.2", {"start": v(37.87, -0.34) * mm, "end": v(36.4, -0.44) * mm});
            skLineSegment(sketch, "E54.18.3", {"start": v(37.54, 4.63) * mm, "end": v(36.06, 4.53) * mm});
            skPoint(sketch, "E54.18.4", {"position": v(41.25, 1.64) * mm});
            skPoint(sketch, "E54.18.5", {"position": v(41.15, 3.1) * mm});
            skArc(sketch, "E54.18.6", {"start": v(38.06, 4.58) * mm, "mid": v(39.57, 4.03) * mm, "end": v(40.97, 3.23) * mm});
            skPoint(sketch, "E54.18.7", {"position": v(37.8, 4.65) * mm});
            skPoint(sketch, "E54.18.8", {"position": v(38.12, -0.33) * mm});
            skArc(sketch, "E54.18.9", {"start": v(38.38, -0.22) * mm, "mid": v(39.8, 0.52) * mm, "end": v(41.08, 1.49) * mm});
            skLineSegment(sketch, "E54.18.10", {"start": v(41.25, 1.87) * mm, "end": v(41.25, 2.37) * mm});
            skLineSegment(sketch, "E54.18.11", {"start": v(41.18, 2.88) * mm, "end": v(41.25, 2.37) * mm});
            skArc(sketch, "E54.18.12", {"start": v(37.87, -0.34) * mm, "mid": v(38.13, -0.3) * mm, "end": v(38.38, -0.22) * mm});
            skArc(sketch, "E54.18.13", {"start": v(41.18, 2.88) * mm, "mid": v(41.11, 3.08) * mm, "end": v(40.97, 3.23) * mm});
            skArc(sketch, "E54.18.14", {"start": v(38.06, 4.58) * mm, "mid": v(37.8, 4.62) * mm, "end": v(37.54, 4.63) * mm});
            skArc(sketch, "E54.18.15", {"start": v(41.08, 1.49) * mm, "mid": v(41.2, 1.66) * mm, "end": v(41.25, 1.87) * mm});
            skArc(sketch, "E54.19.0", {"start": v(35.18, 8.98) * mm, "mid": v(34.3, 8.25) * mm, "end": v(34.14, 7.13) * mm});
            skArc(sketch, "E54.19.1", {"start": v(31.63, 14.52) * mm, "mid": v(32.45, 13.74) * mm, "end": v(33.58, 13.7) * mm});
            skLineSegment(sketch, "E54.19.2", {"start": v(36.58, 9.45) * mm, "end": v(35.18, 8.98) * mm});
            skLineSegment(sketch, "E54.19.3", {"start": v(34.98, 14.17) * mm, "end": v(33.58, 13.7) * mm});
            skPoint(sketch, "E54.19.4", {"position": v(39.33, 12.25) * mm});
            skPoint(sketch, "E54.19.5", {"position": v(38.87, 13.63) * mm});
            skArc(sketch, "E54.19.6", {"start": v(35.5, 14.26) * mm, "mid": v(37.1, 14.11) * mm, "end": v(38.65, 13.7) * mm});
            skPoint(sketch, "E54.19.7", {"position": v(35.22, 14.25) * mm});
            skPoint(sketch, "E54.19.8", {"position": v(36.82, 9.53) * mm});
            skArc(sketch, "E54.19.9", {"start": v(37.04, 9.7) * mm, "mid": v(38.23, 10.78) * mm, "end": v(39.21, 12.05) * mm});
            skLineSegment(sketch, "E54.19.10", {"start": v(39.28, 12.46) * mm, "end": v(39.15, 12.95) * mm});
            skLineSegment(sketch, "E54.19.11", {"start": v(38.95, 13.42) * mm, "end": v(39.15, 12.95) * mm});
            skArc(sketch, "E54.19.12", {"start": v(36.58, 9.45) * mm, "mid": v(36.82, 9.56) * mm, "end": v(37.04, 9.7) * mm});
            skArc(sketch, "E54.19.13", {"start": v(38.95, 13.42) * mm, "mid": v(38.83, 13.6) * mm, "end": v(38.65, 13.7) * mm});
            skArc(sketch, "E54.19.14", {"start": v(35.5, 14.26) * mm, "mid": v(35.24, 14.23) * mm, "end": v(34.98, 14.17) * mm});
            skArc(sketch, "E54.19.15", {"start": v(39.21, 12.05) * mm, "mid": v(39.29, 12.25) * mm, "end": v(39.28, 12.46) * mm});
            skArc(sketch, "E54.20.0", {"start": v(31.57, 17.76) * mm, "mid": v(30.92, 16.83) * mm, "end": v(31.05, 15.7) * mm});
            skArc(sketch, "E54.20.1", {"start": v(26.71, 22.2) * mm, "mid": v(27.7, 21.65) * mm, "end": v(28.8, 21.9) * mm});
            skLineSegment(sketch, "E54.20.2", {"start": v(32.8, 18.58) * mm, "end": v(31.57, 17.76) * mm});
            skLineSegment(sketch, "E54.20.3", {"start": v(30.04, 22.73) * mm, "end": v(28.8, 21.9) * mm});
            skPoint(sketch, "E54.20.4", {"position": v(34.74, 22) * mm});
            skPoint(sketch, "E54.20.5", {"position": v(33.93, 23.2) * mm});
            skArc(sketch, "E54.20.6", {"start": v(30.51, 22.94) * mm, "mid": v(32.1, 23.22) * mm, "end": v(33.7, 23.23) * mm});
            skPoint(sketch, "E54.20.7", {"position": v(30.25, 22.87) * mm});
            skPoint(sketch, "E54.20.8", {"position": v(33.02, 18.72) * mm});
            skArc(sketch, "E54.20.9", {"start": v(33.19, 18.94) * mm, "mid": v(34.05, 20.3) * mm, "end": v(34.67, 21.78) * mm});
            skLineSegment(sketch, "E54.20.10", {"start": v(34.63, 22.19) * mm, "end": v(34.37, 22.63) * mm});
            skLineSegment(sketch, "E54.20.11", {"start": v(34.07, 23.03) * mm, "end": v(34.37, 22.63) * mm});
            skArc(sketch, "E54.20.12", {"start": v(32.8, 18.58) * mm, "mid": v(33.01, 18.74) * mm, "end": v(33.19, 18.94) * mm});
            skArc(sketch, "E54.20.13", {"start": v(34.07, 23.03) * mm, "mid": v(33.9, 23.17) * mm, "end": v(33.7, 23.23) * mm});
            skArc(sketch, "E54.20.14", {"start": v(30.51, 22.94) * mm, "mid": v(30.27, 22.85) * mm, "end": v(30.04, 22.73) * mm});
            skArc(sketch, "E54.20.15", {"start": v(34.67, 21.78) * mm, "mid": v(34.7, 21.99) * mm, "end": v(34.63, 22.19) * mm});
            skArc(sketch, "E54.21.0", {"start": v(25.82, 25.3) * mm, "mid": v(25.42, 24.25) * mm, "end": v(25.84, 23.2) * mm});
            skArc(sketch, "E54.21.1", {"start": v(19.97, 28.34) * mm, "mid": v(21.07, 28.07) * mm, "end": v(22.07, 28.6) * mm});
            skLineSegment(sketch, "E54.21.2", {"start": v(26.8, 26.42) * mm, "end": v(25.82, 25.3) * mm});
            skLineSegment(sketch, "E54.21.3", {"start": v(23.05, 29.7) * mm, "end": v(22.07, 28.6) * mm});
            skPoint(sketch, "E54.21.4", {"position": v(27.78, 30.22) * mm});
            skPoint(sketch, "E54.21.5", {"position": v(26.68, 31.18) * mm});
            skArc(sketch, "E54.21.6", {"start": v(23.45, 30.04) * mm, "mid": v(24.9, 30.72) * mm, "end": v(26.46, 31.14) * mm});
            skPoint(sketch, "E54.21.7", {"position": v(23.22, 29.9) * mm});
            skPoint(sketch, "E54.21.8", {"position": v(26.96, 26.61) * mm});
            skArc(sketch, "E54.21.9", {"start": v(27.07, 26.87) * mm, "mid": v(27.55, 28.4) * mm, "end": v(27.77, 30) * mm});
            skLineSegment(sketch, "E54.21.10", {"start": v(27.62, 30.38) * mm, "end": v(27.26, 30.74) * mm});
            skLineSegment(sketch, "E54.21.11", {"start": v(26.86, 31.04) * mm, "end": v(27.26, 30.74) * mm});
            skArc(sketch, "E54.21.12", {"start": v(26.8, 26.42) * mm, "mid": v(26.95, 26.63) * mm, "end": v(27.07, 26.87) * mm});
            skArc(sketch, "E54.21.13", {"start": v(26.86, 31.04) * mm, "mid": v(26.67, 31.14) * mm, "end": v(26.46, 31.14) * mm});
            skArc(sketch, "E54.21.14", {"start": v(23.45, 30.04) * mm, "mid": v(23.24, 29.9) * mm, "end": v(23.05, 29.7) * mm});
            skArc(sketch, "E54.21.15", {"start": v(27.77, 30) * mm, "mid": v(27.74, 30.2) * mm, "end": v(27.62, 30.38) * mm});
            skArc(sketch, "E54.22.0", {"start": v(18.3, 31.11) * mm, "mid": v(18.2, 29.98) * mm, "end": v(18.87, 29.07) * mm});
            skArc(sketch, "E54.22.1", {"start": v(11.87, 32.53) * mm, "mid": v(13, 32.55) * mm, "end": v(13.83, 33.32) * mm});
            skLineSegment(sketch, "E54.22.2", {"start": v(18.96, 32.44) * mm, "end": v(18.3, 31.11) * mm});
            skLineSegment(sketch, "E54.22.3", {"start": v(14.5, 34.65) * mm, "end": v(13.83, 33.32) * mm});
            skPoint(sketch, "E54.22.4", {"position": v(18.93, 36.36) * mm});
            skPoint(sketch, "E54.22.5", {"position": v(17.62, 37) * mm});
            skArc(sketch, "E54.22.6", {"start": v(14.8, 35.07) * mm, "mid": v(16.03, 36.1) * mm, "end": v(17.41, 36.91) * mm});
            skPoint(sketch, "E54.22.7", {"position": v(14.6, 34.87) * mm});
            skPoint(sketch, "E54.22.8", {"position": v(19.07, 32.67) * mm});
            skArc(sketch, "E54.22.9", {"start": v(19.11, 32.94) * mm, "mid": v(19.18, 34.55) * mm, "end": v(18.98, 36.14) * mm});
            skLineSegment(sketch, "E54.22.10", {"start": v(18.74, 36.47) * mm, "end": v(18.3, 36.73) * mm});
            skLineSegment(sketch, "E54.22.11", {"start": v(17.83, 36.92) * mm, "end": v(18.3, 36.73) * mm});
            skArc(sketch, "E54.22.12", {"start": v(18.96, 32.44) * mm, "mid": v(19.06, 32.69) * mm, "end": v(19.11, 32.94) * mm});
            skArc(sketch, "E54.22.13", {"start": v(17.83, 36.92) * mm, "mid": v(17.62, 36.96) * mm, "end": v(17.41, 36.91) * mm});
            skArc(sketch, "E54.22.14", {"start": v(14.8, 35.07) * mm, "mid": v(14.63, 34.87) * mm, "end": v(14.5, 34.65) * mm});
            skArc(sketch, "E54.22.15", {"start": v(18.98, 36.14) * mm, "mid": v(18.9, 36.33) * mm, "end": v(18.74, 36.47) * mm});
            skArc(sketch, "E54.23.0", {"start": v(9.54, 34.77) * mm, "mid": v(9.73, 33.66) * mm, "end": v(10.62, 32.95) * mm});
            skArc(sketch, "E54.23.1", {"start": v(2.97, 34.47) * mm, "mid": v(4.05, 34.79) * mm, "end": v(4.66, 35.74) * mm});
            skLineSegment(sketch, "E54.23.2", {"start": v(9.83, 36.23) * mm, "end": v(9.54, 34.77) * mm});
            skLineSegment(sketch, "E54.23.3", {"start": v(4.95, 37.2) * mm, "end": v(4.66, 35.74) * mm});
            skPoint(sketch, "E54.23.4", {"position": v(8.79, 40) * mm});
            skPoint(sketch, "E54.23.5", {"position": v(7.36, 40.29) * mm});
            skArc(sketch, "E54.23.6", {"start": v(5.13, 37.69) * mm, "mid": v(6.05, 39) * mm, "end": v(7.18, 40.14) * mm});
            skPoint(sketch, "E54.23.7", {"position": v(5, 37.45) * mm});
            skPoint(sketch, "E54.23.8", {"position": v(9.88, 36.47) * mm});
            skArc(sketch, "E54.23.9", {"start": v(9.85, 36.75) * mm, "mid": v(9.5, 38.32) * mm, "end": v(8.9, 39.8) * mm});
            skLineSegment(sketch, "E54.23.10", {"start": v(8.57, 40.06) * mm, "end": v(8.08, 40.2) * mm});
            skLineSegment(sketch, "E54.23.11", {"start": v(7.58, 40.26) * mm, "end": v(8.08, 40.2) * mm});
            skArc(sketch, "E54.23.12", {"start": v(9.83, 36.23) * mm, "mid": v(9.86, 36.49) * mm, "end": v(9.85, 36.75) * mm});
            skArc(sketch, "E54.23.13", {"start": v(7.58, 40.26) * mm, "mid": v(7.37, 40.24) * mm, "end": v(7.18, 40.14) * mm});
            skArc(sketch, "E54.23.14", {"start": v(5.13, 37.69) * mm, "mid": v(5.02, 37.45) * mm, "end": v(4.95, 37.2) * mm});
            skArc(sketch, "E54.23.15", {"start": v(8.9, 39.8) * mm, "mid": v(8.76, 39.97) * mm, "end": v(8.57, 40.06) * mm});
            skArc(sketch, "E55.trimOffspring", {"start": v(-14.83, 31.28) * mm, "mid": v(-15.43, 31) * mm, "end": v(-16.02, 30.7) * mm});
            skArc(sketch, "E56.trimOffspring", {"start": v(-22.5, 26.36) * mm, "mid": v(-23, 25.93) * mm, "end": v(-23.5, 25.49) * mm});
            skArc(sketch, "E57.trimOffspring", {"start": v(-28.64, 19.62) * mm, "mid": v(-29.02, 19.08) * mm, "end": v(-29.38, 18.52) * mm});
            skArc(sketch, "E58.trimOffspring", {"start": v(-32.83, 11.52) * mm, "mid": v(-33.05, 10.9) * mm, "end": v(-33.26, 10.27) * mm});
            skArc(sketch, "E59.trimOffspring", {"start": v(-34.78, 2.62) * mm, "mid": v(-34.83, 1.96) * mm, "end": v(-34.87, 1.3) * mm});
            skArc(sketch, "E60.trimOffspring", {"start": v(-34.36, -6.5) * mm, "mid": v(-34.23, -7.14) * mm, "end": v(-34.1, -7.79) * mm});
            skArc(sketch, "E61.trimOffspring", {"start": v(-31.59, -15.18) * mm, "mid": v(-31.3, -15.77) * mm, "end": v(-31, -16.37) * mm});
            skArc(sketch, "E62.trimOffspring", {"start": v(-26.67, -22.85) * mm, "mid": v(-26.24, -23.36) * mm, "end": v(-25.8, -23.85) * mm});
            skArc(sketch, "E63.trimOffspring", {"start": v(-19.93, -29) * mm, "mid": v(-19.38, -29.37) * mm, "end": v(-18.83, -29.73) * mm});
            skArc(sketch, "E64.trimOffspring", {"start": v(-11.83, -33.18) * mm, "mid": v(-11.2, -33.4) * mm, "end": v(-10.58, -33.6) * mm});
            skArc(sketch, "E65.trimOffspring", {"start": v(-2.92, -35.13) * mm, "mid": v(-2.26, -35.18) * mm, "end": v(-1.6, -35.22) * mm});
            skArc(sketch, "E66.trimOffspring", {"start": v(6.19, -34.7) * mm, "mid": v(6.84, -34.58) * mm, "end": v(7.48, -34.45) * mm});
            skArc(sketch, "E67.trimOffspring", {"start": v(14.87, -31.94) * mm, "mid": v(15.47, -31.65) * mm, "end": v(16.06, -31.35) * mm});
            skArc(sketch, "E68.trimOffspring", {"start": v(22.55, -27.02) * mm, "mid": v(23.05, -26.59) * mm, "end": v(23.54, -26.15) * mm});
            skArc(sketch, "E69.trimOffspring", {"start": v(28.69, -20.28) * mm, "mid": v(29.06, -19.73) * mm, "end": v(29.42, -19.18) * mm});
            skArc(sketch, "E70.trimOffspring", {"start": v(32.87, -12.18) * mm, "mid": v(33.1, -11.55) * mm, "end": v(33.3, -10.93) * mm});
            skArc(sketch, "E71.trimOffspring", {"start": v(34.82, -3.27) * mm, "mid": v(34.87, -2.61) * mm, "end": v(34.9, -1.95) * mm});
            skArc(sketch, "E72.trimOffspring", {"start": v(34.4, 5.84) * mm, "mid": v(34.28, 6.49) * mm, "end": v(34.14, 7.13) * mm});
            skArc(sketch, "E73.trimOffspring", {"start": v(31.63, 14.52) * mm, "mid": v(31.34, 15.12) * mm, "end": v(31.05, 15.7) * mm});
            skArc(sketch, "E74.trimOffspring", {"start": v(26.71, 22.2) * mm, "mid": v(26.28, 22.7) * mm, "end": v(25.84, 23.2) * mm});
            skArc(sketch, "E75.trimOffspring", {"start": v(19.97, 28.34) * mm, "mid": v(19.42, 28.71) * mm, "end": v(18.87, 29.07) * mm});
            skArc(sketch, "E76.trimOffspring", {"start": v(11.87, 32.53) * mm, "mid": v(11.25, 32.74) * mm, "end": v(10.62, 32.95) * mm});
            skArc(sketch, "E77.trimOffspring", {"start": v(2.97, 34.47) * mm, "mid": v(2.3, 34.52) * mm, "end": v(1.65, 34.56) * mm});
            skSolve(sketch);
        }
        {
            var Q0;
            Q0 = qSketchRegion(id + "F0", true);
            var Q1;
            Q1=makeQuery(id+"F2.imprint","IMPRINT",FACE,{"disambiguationData":[TD([[makeQuery(id+"F2.imprint","IMPRINT",EDGE,{"derivedFrom":sQuery(id+"F2.wireOp",EDGE,"E39")}),1.0]])]});
            var Q2;
            Q2=sQuery(id+"F0.wireOp",VERTEX,"E15.23.11.end");
            var Q3;
            Q3=sQuery(id+"F2.wireOp",VERTEX,"E54.22.11.end");
            loft(context, id + "F3", {"sheetProfilesArray" : [{ "sheetProfileEntities" : qUnion([Q0]) }, { "sheetProfileEntities" : qUnion([Q1]) }], "matchConnections" : true, "connections" : [{ "connectionEntities" : qUnion([Q2, Q3]), "connectionEdgeQueries" : qUnion([]), "connectionEdgeParameters" : [] }]});
        }
        {
            var Q0;
            Q0=sQuery(id+"F2.wireOp",VERTEX,"E39.center");
            var Q1;
            Q1=makeQuery(id+"F3.opLoft","SWEPT_BODY",BODY,{"disambiguationData":[OSD([makeQuery(id+"F0.imprint","IMPRINT",FACE,{"disambiguationData":[TD([[makeQuery(id+"F0.imprint","IMPRINT",EDGE,{"derivedFrom":sQuery(id+"F0.wireOp",EDGE,"E0")}),1.0]])]}),makeQuery(id+"F2.imprint","IMPRINT",FACE,{"disambiguationData":[TD([[makeQuery(id+"F2.imprint","IMPRINT",EDGE,{"derivedFrom":sQuery(id+"F2.wireOp",EDGE,"E39")}),1.0]])]})])]});
            hole(context, id + "F4", {"style" : HoleStyle.SIMPLE, "endStyle" : HoleEndStyle.BLIND, "holeDiameter" : 12.7 * mm, "holeDepth" : 50.8 * mm, "tappedDepth" : 12.7 * mm, "tapClearance" : 3, "locations" : qUnion([Q0]), "scope" : qUnion([Q1])});
        }
    });
